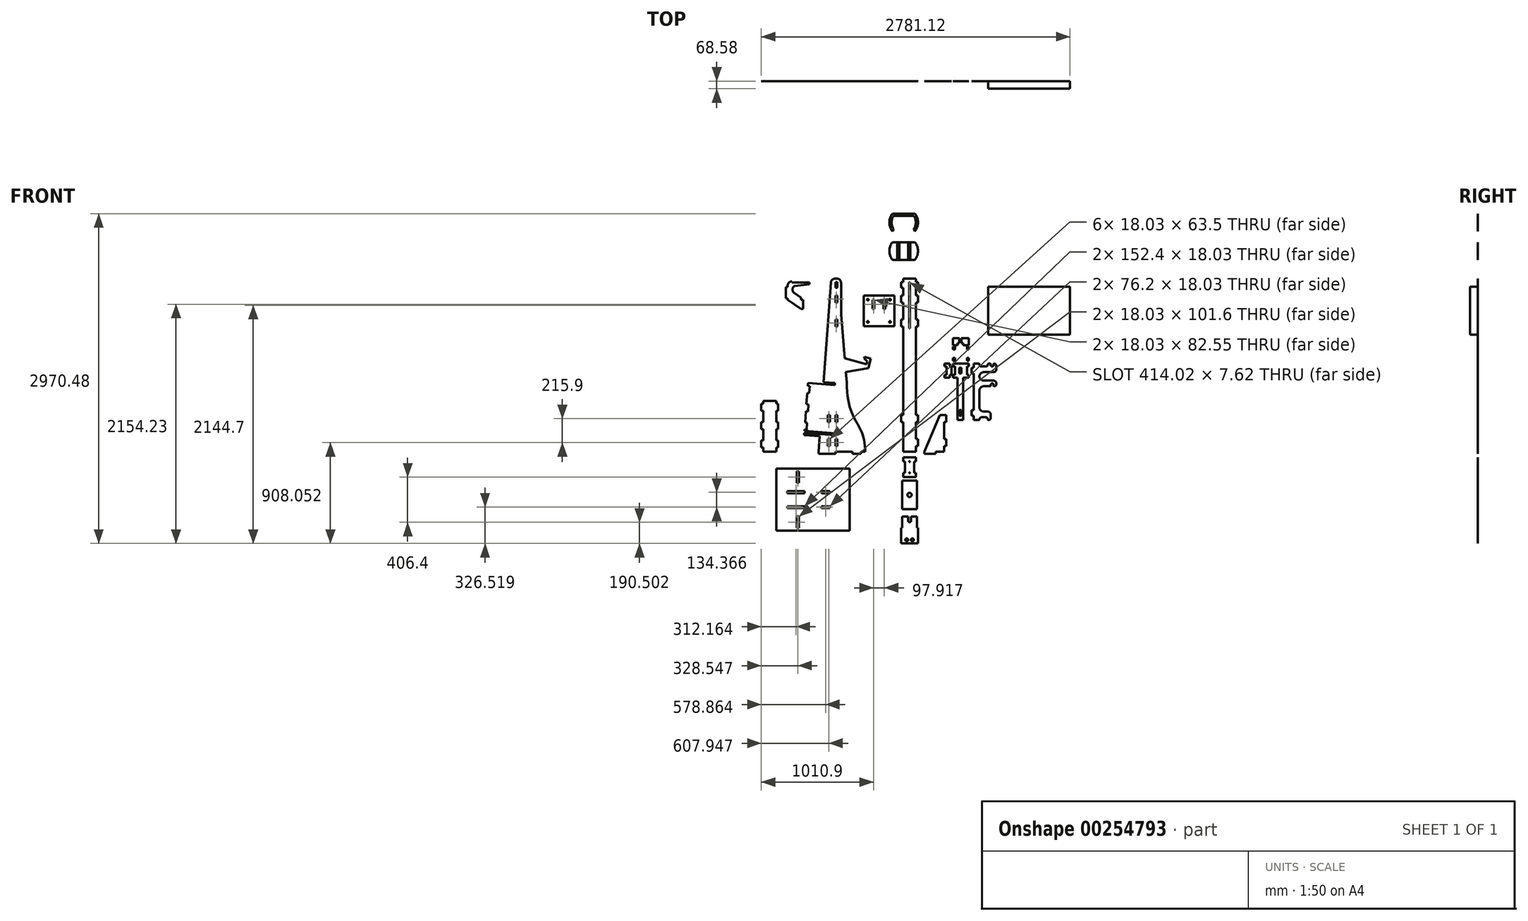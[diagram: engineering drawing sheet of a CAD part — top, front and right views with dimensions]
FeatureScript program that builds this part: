
annotation { "Feature Type Name" : "Feature", "Feature Type Description" : "" }
export const myFeature = defineFeature(function(context is Context, id is Id, definition is map)
    precondition{}
    {
        {
            assignVariable(context, id + "F0", {"name" : "ply34", "anyValue" : .71});
        }
        {
            var Q0;
            Q0=qCreatedBy(makeId("Front.planeOp"),FACE);
            var sketch = newSketch(context, id + "F1", { "sketchPlane" : qUnion([Q0])});
            skLineSegment(sketch, "E0.bottom", {"start": v(-58.17, 729.59) * mm, "end": v(58.17, 729.59) * mm, "construction": true});
            skLineSegment(sketch, "E0.top", {"start": v(-58.17, -729.59) * mm, "end": v(58.17, -729.59) * mm});
            skLineSegment(sketch, "E0.left", {"start": v(-58.17, 729.59) * mm, "end": v(-58.17, -729.59) * mm});
            skLineSegment(sketch, "E0.right", {"start": v(58.17, 729.59) * mm, "end": v(58.17, -729.59) * mm});
            skPoint(sketch, "E0.middle", {"position": v(0, 0) * mm});
            skLineSegment(sketch, "E1.bottom", {"start": v(76.2, 678.79) * mm, "end": v(58.17, 678.79) * mm});
            skLineSegment(sketch, "E1.top", {"start": v(76.2, 615.29) * mm, "end": v(58.17, 615.29) * mm});
            skLineSegment(sketch, "E1.left", {"start": v(58.17, 678.79) * mm, "end": v(58.17, 615.29) * mm});
            skLineSegment(sketch, "E1.right", {"start": v(76.2, 678.79) * mm, "end": v(76.2, 615.29) * mm});
            skPoint(sketch, "E2.oppositeSnap0", {"position": v(76.2, 647.04) * mm});
            skLineSegment(sketch, "E2.bottom", {"start": v(76.2, 462.89) * mm, "end": v(58.17, 462.89) * mm});
            skLineSegment(sketch, "E2.top", {"start": v(76.2, 399.39) * mm, "end": v(58.17, 399.39) * mm});
            skLineSegment(sketch, "E2.left", {"start": v(58.17, 462.89) * mm, "end": v(58.17, 399.39) * mm});
            skLineSegment(sketch, "E2.right", {"start": v(76.2, 462.89) * mm, "end": v(76.2, 399.39) * mm});
            skLineSegment(sketch, "E3", {"start": v(-58.17, 0) * mm, "end": v(58.17, 0) * mm, "construction": true});
            skLineSegment(sketch, "E4", {"start": v(0, 729.59) * mm, "end": v(0, 0) * mm, "construction": true});
            skLineSegment(sketch, "E5.MirrorCS", {"start": v(76.2, -678.79) * mm, "end": v(58.17, -678.79) * mm});
            skLineSegment(sketch, "E6.MirrorCS", {"start": v(76.2, -615.29) * mm, "end": v(58.17, -615.29) * mm});
            skLineSegment(sketch, "E7.MirrorCS", {"start": v(76.2, -462.89) * mm, "end": v(58.17, -462.89) * mm});
            skLineSegment(sketch, "E8.MirrorCS", {"start": v(76.2, -399.39) * mm, "end": v(58.17, -399.39) * mm});
            skPoint(sketch, "E9.MirrorP", {"position": v(76.2, -647.04) * mm});
            skLineSegment(sketch, "E10.MirrorCS", {"start": v(58.17, -678.79) * mm, "end": v(58.17, -615.29) * mm});
            skLineSegment(sketch, "E11.MirrorCS", {"start": v(76.2, -678.79) * mm, "end": v(76.2, -615.29) * mm});
            skLineSegment(sketch, "E12.MirrorCS", {"start": v(76.2, -462.89) * mm, "end": v(76.2, -399.39) * mm});
            skLineSegment(sketch, "E13.MirrorCS", {"start": v(58.17, -462.89) * mm, "end": v(58.17, -399.39) * mm});
            skLineSegment(sketch, "E14.MirrorCS", {"start": v(-76.2, -462.89) * mm, "end": v(-58.17, -462.89) * mm});
            skLineSegment(sketch, "E15.MirrorCS", {"start": v(-58.17, -678.79) * mm, "end": v(-58.17, -615.29) * mm});
            skLineSegment(sketch, "E16.MirrorCS", {"start": v(-76.2, 462.89) * mm, "end": v(-76.2, 399.39) * mm});
            skLineSegment(sketch, "E17.MirrorCS", {"start": v(-58.17, 462.89) * mm, "end": v(-58.17, 399.39) * mm});
            skLineSegment(sketch, "E18.MirrorCS", {"start": v(-76.2, 399.39) * mm, "end": v(-58.17, 399.39) * mm});
            skLineSegment(sketch, "E19.MirrorCS", {"start": v(-76.2, 462.89) * mm, "end": v(-58.17, 462.89) * mm});
            skLineSegment(sketch, "E20.MirrorCS", {"start": v(-76.2, 678.79) * mm, "end": v(-76.2, 615.29) * mm});
            skLineSegment(sketch, "E21.MirrorCS", {"start": v(-58.17, 678.79) * mm, "end": v(-58.17, 615.29) * mm});
            skLineSegment(sketch, "E22.MirrorCS", {"start": v(-76.2, -615.29) * mm, "end": v(-58.17, -615.29) * mm});
            skLineSegment(sketch, "E23.MirrorCS", {"start": v(-76.2, -678.79) * mm, "end": v(-58.17, -678.79) * mm});
            skLineSegment(sketch, "E24.MirrorCS", {"start": v(-76.2, 615.29) * mm, "end": v(-58.17, 615.29) * mm});
            skLineSegment(sketch, "E25.MirrorCS", {"start": v(-76.2, -399.39) * mm, "end": v(-58.17, -399.39) * mm});
            skLineSegment(sketch, "E26.MirrorCS", {"start": v(-76.2, -678.79) * mm, "end": v(-76.2, -615.29) * mm});
            skLineSegment(sketch, "E27.MirrorCS", {"start": v(-76.2, 678.79) * mm, "end": v(-58.17, 678.79) * mm});
            skLineSegment(sketch, "E28.MirrorCS", {"start": v(-76.2, -462.89) * mm, "end": v(-76.2, -399.39) * mm});
            skPoint(sketch, "E29.MirrorP", {"position": v(-76.2, -647.04) * mm});
            skPoint(sketch, "E30.MirrorP", {"position": v(-76.2, 647.04) * mm});
            skLineSegment(sketch, "E31.MirrorCS", {"start": v(-58.17, -462.89) * mm, "end": v(-58.17, -399.39) * mm});
            skLineSegment(sketch, "E32", {"start": v(-667.77, 729.59) * mm, "end": v(-712.22, 729.59) * mm, "construction": true});
            skLineSegment(sketch, "E33", {"start": v(-712.22, 729.59) * mm, "end": v(-820.17, -729.59) * mm});
            skLineSegment(sketch, "E34", {"start": v(-820.17, -729.59) * mm, "end": v(-667.77, -729.59) * mm});
            skLineSegment(sketch, "E35", {"start": v(-667.77, -729.59) * mm, "end": v(-667.77, 729.59) * mm, "construction": true});
            skLineSegment(sketch, "E36", {"start": v(-667.77, -678.79) * mm, "end": v(-649.73, -678.79) * mm});
            skLineSegment(sketch, "E37", {"start": v(-649.73, -678.79) * mm, "end": v(-649.73, -615.29) * mm});
            skLineSegment(sketch, "E38", {"start": v(-649.73, -615.29) * mm, "end": v(-667.77, -615.29) * mm});
            skLineSegment(sketch, "E39", {"start": v(-667.77, -462.89) * mm, "end": v(-649.73, -462.89) * mm});
            skLineSegment(sketch, "E40", {"start": v(-649.73, -462.89) * mm, "end": v(-649.73, -399.39) * mm});
            skLineSegment(sketch, "E41", {"start": v(-649.73, -399.39) * mm, "end": v(-667.77, -399.39) * mm});
            skLineSegment(sketch, "E42.MirrorCS", {"start": v(-667.77, 678.79) * mm, "end": v(-649.73, 678.79) * mm});
            skLineSegment(sketch, "E43.MirrorCS", {"start": v(-649.73, 399.39) * mm, "end": v(-667.77, 399.39) * mm});
            skLineSegment(sketch, "E44.MirrorCS", {"start": v(-667.77, 462.89) * mm, "end": v(-649.73, 462.89) * mm});
            skLineSegment(sketch, "E45.MirrorCS", {"start": v(-649.73, 615.29) * mm, "end": v(-667.77, 615.29) * mm});
            skLineSegment(sketch, "E46.MirrorCS", {"start": v(-649.73, 678.79) * mm, "end": v(-649.73, 615.29) * mm});
            skLineSegment(sketch, "E47.MirrorCS", {"start": v(-649.73, 462.89) * mm, "end": v(-649.73, 399.39) * mm});
            skLineSegment(sketch, "E48.bottom", {"start": v(-718.57, -462.89) * mm, "end": v(-736.6, -462.89) * mm});
            skLineSegment(sketch, "E48.top", {"start": v(-718.57, -399.39) * mm, "end": v(-736.6, -399.39) * mm});
            skLineSegment(sketch, "E48.left", {"start": v(-718.57, -462.89) * mm, "end": v(-718.57, -399.39) * mm});
            skLineSegment(sketch, "E48.right", {"start": v(-736.6, -462.89) * mm, "end": v(-736.6, -399.39) * mm});
            skPoint(sketch, "E48.middle", {"position": v(-727.58, -431.14) * mm});
            skPoint(sketch, "E48.middle.positionSnap0", {"position": v(-649.73, -431.14) * mm});
            skPoint(sketch, "E48.middle.positionSnap1", {"position": v(-743.97, -729.59) * mm});
            skPoint(sketch, "E48.centerSnap0", {"position": v(-649.73, -431.14) * mm});
            skPoint(sketch, "E48.centerSnap1", {"position": v(-743.97, -729.59) * mm});
            skLineSegment(sketch, "E49.bottom", {"start": v(-718.57, -615.29) * mm, "end": v(-736.6, -615.29) * mm});
            skLineSegment(sketch, "E49.top", {"start": v(-718.57, -678.79) * mm, "end": v(-736.6, -678.79) * mm});
            skLineSegment(sketch, "E49.left", {"start": v(-718.57, -615.29) * mm, "end": v(-718.57, -678.79) * mm});
            skLineSegment(sketch, "E49.right", {"start": v(-736.6, -615.29) * mm, "end": v(-736.6, -678.79) * mm});
            skPoint(sketch, "E49.middle", {"position": v(-727.58, -647.04) * mm});
            skPoint(sketch, "E49.middle.positionSnap0", {"position": v(-649.73, -647.04) * mm});
            skPoint(sketch, "E49.cornerSnap0", {"position": v(-718.57, -431.14) * mm});
            skPoint(sketch, "E49.centerSnap0", {"position": v(-649.73, -647.04) * mm});
            skLineSegment(sketch, "E50", {"start": v(-793.93, -374.96) * mm, "end": v(-775.95, -376.29) * mm, "construction": true});
            skLineSegment(sketch, "E51", {"start": v(-775.95, -376.29) * mm, "end": v(-771.26, -312.96) * mm, "construction": true});
            skLineSegment(sketch, "E52", {"start": v(-771.26, -312.96) * mm, "end": v(-789.25, -311.63) * mm, "construction": true});
            skLineSegment(sketch, "E53", {"start": v(-781.75, -210.3) * mm, "end": v(-763.76, -211.64) * mm, "construction": true});
            skLineSegment(sketch, "E54", {"start": v(-763.76, -211.64) * mm, "end": v(-759.08, -148.31) * mm, "construction": true});
            skLineSegment(sketch, "E55", {"start": v(-759.08, -148.31) * mm, "end": v(-777.06, -146.98) * mm, "construction": true});
            skLineSegment(sketch, "E56.bottom", {"start": v(-1201.17, -729.59) * mm, "end": v(-1317.5, -729.59) * mm});
            skLineSegment(sketch, "E56.top", {"start": v(-1201.17, -272.39) * mm, "end": v(-1317.5, -272.39) * mm});
            skLineSegment(sketch, "E56.left", {"start": v(-1201.17, -729.59) * mm, "end": v(-1201.17, -272.39) * mm});
            skLineSegment(sketch, "E56.right", {"start": v(-1317.5, -729.59) * mm, "end": v(-1317.5, -272.39) * mm});
            skLineSegment(sketch, "E57.bottom", {"start": v(-1183.13, -526.39) * mm, "end": v(-1201.17, -526.39) * mm});
            skLineSegment(sketch, "E57.top", {"start": v(-1183.13, -462.89) * mm, "end": v(-1201.17, -462.89) * mm});
            skLineSegment(sketch, "E57.right", {"start": v(-1183.13, -526.39) * mm, "end": v(-1183.13, -462.89) * mm});
            skLineSegment(sketch, "E58", {"start": v(-1259.33, -272.39) * mm, "end": v(-1259.33, -729.59) * mm, "construction": true});
            skLineSegment(sketch, "E59.MirrorCS", {"start": v(-1183.13, -297.79) * mm, "end": v(-1201.17, -297.79) * mm});
            skLineSegment(sketch, "E60.MirrorCS", {"start": v(-1183.13, -297.79) * mm, "end": v(-1183.13, -361.29) * mm});
            skLineSegment(sketch, "E61.MirrorCS", {"start": v(-1183.13, -361.29) * mm, "end": v(-1201.17, -361.29) * mm});
            skLineSegment(sketch, "E62.MirrorCS", {"start": v(-1335.53, -526.39) * mm, "end": v(-1335.53, -462.89) * mm});
            skLineSegment(sketch, "E63.MirrorCS", {"start": v(-1335.53, -462.89) * mm, "end": v(-1317.5, -462.89) * mm});
            skLineSegment(sketch, "E64.MirrorCS", {"start": v(-1335.53, -361.29) * mm, "end": v(-1317.5, -361.29) * mm});
            skLineSegment(sketch, "E65.MirrorCS", {"start": v(-1335.53, -526.39) * mm, "end": v(-1317.5, -526.39) * mm});
            skLineSegment(sketch, "E66.MirrorCS", {"start": v(-1335.53, -297.79) * mm, "end": v(-1335.53, -361.29) * mm});
            skLineSegment(sketch, "E67.MirrorCS", {"start": v(-1335.53, -297.79) * mm, "end": v(-1317.5, -297.79) * mm});
            skLineSegment(sketch, "E68", {"start": v(312.17, -399.39) * mm, "end": v(274.07, -399.39) * mm});
            skLineSegment(sketch, "E69", {"start": v(274.07, -399.39) * mm, "end": v(134.37, -729.59) * mm});
            skLineSegment(sketch, "E70", {"start": v(134.37, -729.59) * mm, "end": v(312.17, -729.59) * mm});
            skLineSegment(sketch, "E71", {"start": v(312.17, -729.59) * mm, "end": v(312.17, -399.39) * mm});
            skLineSegment(sketch, "E72", {"start": v(312.17, -399.39) * mm, "end": v(330.2, -399.39) * mm});
            skLineSegment(sketch, "E73", {"start": v(330.2, -399.39) * mm, "end": v(330.2, -462.89) * mm});
            skLineSegment(sketch, "E74", {"start": v(330.2, -462.89) * mm, "end": v(312.17, -462.89) * mm});
            skLineSegment(sketch, "E75", {"start": v(312.17, -615.29) * mm, "end": v(330.2, -615.29) * mm});
            skLineSegment(sketch, "E76", {"start": v(330.2, -615.29) * mm, "end": v(330.2, -678.79) * mm});
            skLineSegment(sketch, "E77", {"start": v(330.2, -678.79) * mm, "end": v(312.17, -678.79) * mm});
            skLineSegment(sketch, "E78", {"start": v(-667.77, 729.59) * mm, "end": v(-629.67, 729.59) * mm, "construction": true});
            skLineSegment(sketch, "E79", {"start": v(-712.22, 729.59) * mm, "end": v(-707.33, 795.62) * mm});
            skLineSegment(sketch, "E80", {"start": v(-669.33, 830.91) * mm, "end": v(-464.57, 830.91) * mm, "construction": true});
            skLineSegment(sketch, "E81", {"start": v(-464.57, 830.91) * mm, "end": v(-464.57, 780.11) * mm, "construction": true});
            skLineSegment(sketch, "E82", {"start": v(-464.57, 780.11) * mm, "end": v(-616.97, 761.06) * mm, "construction": true});
            skLineSegment(sketch, "E83", {"start": v(-509.38, 438.81) * mm, "end": v(-475.02, 438.81) * mm, "construction": true});
            skLineSegment(sketch, "E84", {"start": v(-616.97, 761.06) * mm, "end": v(-616.97, 659.46) * mm});
            skLineSegment(sketch, "E85", {"start": v(-616.97, 659.46) * mm, "end": v(-515.37, 659.46) * mm, "construction": true});
            skLineSegment(sketch, "E86.bottom", {"start": v(-515.37, 659.46) * mm, "end": v(-533.4, 659.46) * mm, "construction": true});
            skLineSegment(sketch, "E86.top", {"start": v(-515.37, 640.41) * mm, "end": v(-533.4, 640.41) * mm, "construction": true});
            skLineSegment(sketch, "E86.left", {"start": v(-515.37, 659.46) * mm, "end": v(-515.37, 640.41) * mm, "construction": true});
            skLineSegment(sketch, "E86.right", {"start": v(-533.4, 659.46) * mm, "end": v(-533.4, 640.41) * mm, "construction": true});
            skLineSegment(sketch, "E87", {"start": v(-515.37, 659.46) * mm, "end": v(-515.37, 557.86) * mm, "construction": true});
            skLineSegment(sketch, "E88", {"start": v(-616.97, 507.06) * mm, "end": v(-566.17, -102.54) * mm});
            skPoint(sketch, "E88.endSnap0", {"position": v(-566.17, 659.46) * mm});
            skLineSegment(sketch, "E89.0", {"start": v(-547.12, 586.68) * mm, "end": v(-616.97, 544.22) * mm, "construction": true});
            skLineSegment(sketch, "E89.1", {"start": v(-547.12, 627.71) * mm, "end": v(-547.12, 586.68) * mm, "construction": true});
            skLineSegment(sketch, "E89.2", {"start": v(-616.97, 627.71) * mm, "end": v(-547.12, 627.71) * mm, "construction": true});
            skLineSegment(sketch, "E90", {"start": v(-616.97, 627.71) * mm, "end": v(-616.97, 544.22) * mm});
            skLineSegment(sketch, "E91", {"start": v(-667.77, 678.79) * mm, "end": v(-667.77, 615.29) * mm});
            skLineSegment(sketch, "E92", {"start": v(-667.77, 462.89) * mm, "end": v(-667.77, 399.39) * mm});
            skLineSegment(sketch, "E93", {"start": v(-667.77, -399.39) * mm, "end": v(-667.77, -462.89) * mm});
            skLineSegment(sketch, "E94", {"start": v(-667.77, -615.29) * mm, "end": v(-667.77, -678.79) * mm});
            skLineSegment(sketch, "E95", {"start": v(-667.77, -729.59) * mm, "end": v(-439.17, -729.59) * mm});
            skLineSegment(sketch, "E96", {"start": v(-583.98, 111.27) * mm, "end": v(-387.7, 58.68) * mm});
            skLineSegment(sketch, "E97", {"start": v(-387.7, 58.68) * mm, "end": v(-381.13, 83.21) * mm});
            skLineSegment(sketch, "E98", {"start": v(-370.57, 24.5) * mm, "end": v(-576.75, 24.5) * mm, "construction": true});
            skLineSegment(sketch, "E99", {"start": v(-370.57, 24.5) * mm, "end": v(-573.77, -11.33) * mm});
            skLineSegment(sketch, "E100.bottom", {"start": v(-375.67, 640.41) * mm, "end": v(-175.67, 640.41) * mm, "construction": true});
            skLineSegment(sketch, "E100.top", {"start": v(-375.67, 440.41) * mm, "end": v(-175.67, 440.41) * mm, "construction": true});
            skLineSegment(sketch, "E100.left", {"start": v(-375.67, 640.41) * mm, "end": v(-375.67, 440.41) * mm, "construction": true});
            skLineSegment(sketch, "E100.right", {"start": v(-175.67, 640.41) * mm, "end": v(-175.67, 440.41) * mm, "construction": true});
            skLineSegment(sketch, "E101.0", {"start": v(-413.77, 678.51) * mm, "end": v(-137.57, 678.51) * mm});
            skLineSegment(sketch, "E101.1", {"start": v(-413.77, 678.51) * mm, "end": v(-413.77, 402.31) * mm});
            skLineSegment(sketch, "E101.2", {"start": v(-413.77, 402.31) * mm, "end": v(-137.57, 402.31) * mm});
            skLineSegment(sketch, "E101.3", {"start": v(-137.57, 678.51) * mm, "end": v(-137.57, 402.31) * mm});
            skLineSegment(sketch, "E102", {"start": v(-515.37, 557.86) * mm, "end": v(-533.4, 557.86) * mm, "construction": true});
            skLineSegment(sketch, "E103", {"start": v(-533.4, 557.86) * mm, "end": v(-616.97, 507.06) * mm, "construction": true});
            skLineSegment(sketch, "E104.bottom", {"start": v(-333.64, 640.41) * mm, "end": v(-315.6, 640.41) * mm});
            skLineSegment(sketch, "E104.top", {"start": v(-333.64, 557.86) * mm, "end": v(-315.6, 557.86) * mm});
            skLineSegment(sketch, "E104.left", {"start": v(-333.64, 640.41) * mm, "end": v(-333.64, 557.86) * mm});
            skLineSegment(sketch, "E104.right", {"start": v(-315.6, 640.41) * mm, "end": v(-315.6, 557.86) * mm});
            skLineSegment(sketch, "E105", {"start": v(-275.67, 678.51) * mm, "end": v(-275.67, 440.41) * mm, "construction": true});
            skLineSegment(sketch, "E106.MirrorCS", {"start": v(-217.7, 640.41) * mm, "end": v(-235.72, 640.41) * mm});
            skLineSegment(sketch, "E107.MirrorCS", {"start": v(-235.72, 640.41) * mm, "end": v(-235.72, 557.86) * mm});
            skLineSegment(sketch, "E108.MirrorCS", {"start": v(-217.7, 640.41) * mm, "end": v(-217.7, 557.86) * mm});
            skLineSegment(sketch, "E109.MirrorCS", {"start": v(-217.7, 557.86) * mm, "end": v(-235.72, 557.86) * mm});
            skCircle(sketch, "E110", {"center": v(-375.67, 640.41) * mm, "radius": 6.99 * mm});
            skLineSegment(sketch, "E111", {"start": v(-375.67, 540.41) * mm, "end": v(-175.67, 540.41) * mm, "construction": true});
            skCircle(sketch, "E112.MirrorC", {"center": v(-175.67, 640.41) * mm, "radius": 6.99 * mm});
            skCircle(sketch, "E113.MirrorC", {"center": v(-375.67, 440.41) * mm, "radius": 6.99 * mm});
            skCircle(sketch, "E114.MirrorC", {"center": v(-175.67, 440.41) * mm, "radius": 6.99 * mm});
            skLineSegment(sketch, "E115.bottom", {"start": v(-582.04, 830.91) * mm, "end": v(-505.84, 830.91) * mm, "construction": true});
            skLineSegment(sketch, "E115.top", {"start": v(-582.04, 848.95) * mm, "end": v(-505.84, 848.95) * mm, "construction": true});
            skLineSegment(sketch, "E115.left", {"start": v(-582.04, 848.95) * mm, "end": v(-582.04, 830.91) * mm});
            skLineSegment(sketch, "E115.right", {"start": v(-505.84, 848.95) * mm, "end": v(-505.84, 830.91) * mm, "construction": true});
            skLineSegment(sketch, "E116.bottom", {"start": v(-180.97, 983.59) * mm, "end": v(76.2, 983.59) * mm});
            skLineSegment(sketch, "E116.top", {"start": v(-180.97, 1174.09) * mm, "end": v(76.2, 1174.09) * mm});
            skLineSegment(sketch, "E116.left", {"start": v(-180.97, 983.59) * mm, "end": v(-180.97, 1174.09) * mm});
            skLineSegment(sketch, "E116.right", {"start": v(76.2, 983.59) * mm, "end": v(76.2, 1174.09) * mm});
            skLineSegment(sketch, "E117.bottom", {"start": v(-110.36, 1158.21) * mm, "end": v(-92.33, 1158.21) * mm});
            skLineSegment(sketch, "E117.top", {"start": v(-110.36, 999.46) * mm, "end": v(-92.33, 999.46) * mm});
            skLineSegment(sketch, "E117.left", {"start": v(-110.36, 1158.21) * mm, "end": v(-110.36, 999.46) * mm});
            skLineSegment(sketch, "E117.right", {"start": v(-92.33, 1158.21) * mm, "end": v(-92.33, 999.46) * mm});
            skPoint(sketch, "E118.oppositeSnap0", {"position": v(-101.35, 999.46) * mm});
            skLineSegment(sketch, "E118.bottom", {"start": v(-12.45, 1158.21) * mm, "end": v(5.59, 1158.21) * mm});
            skLineSegment(sketch, "E118.top", {"start": v(-12.45, 999.46) * mm, "end": v(5.59, 999.46) * mm});
            skLineSegment(sketch, "E118.left", {"start": v(-12.45, 1158.21) * mm, "end": v(-12.45, 999.46) * mm});
            skLineSegment(sketch, "E118.right", {"start": v(5.59, 1158.21) * mm, "end": v(5.59, 999.46) * mm});
            skLineSegment(sketch, "E119", {"start": v(-92.33, 1078.84) * mm, "end": v(-12.45, 1078.84) * mm, "construction": true});
            skPoint(sketch, "E120", {"position": v(-52.39, 1078.84) * mm});
            skPoint(sketch, "E121", {"position": v(-52.39, 1174.09) * mm});
            skPoint(sketch, "E122", {"position": v(-180.97, 1078.84) * mm});
            skArc(sketch, "E123", {"start": v(-143.82, 1396.34) * mm, "mid": v(-161.92, 1336.01) * mm, "end": v(-143.82, 1275.69) * mm});
            skLineSegment(sketch, "E124.bottom", {"start": v(-143.82, 1396.34) * mm, "end": v(39.04, 1396.34) * mm});
            skLineSegment(sketch, "E124.top", {"start": v(-143.82, 1275.69) * mm, "end": v(39.04, 1275.69) * mm});
            skLineSegment(sketch, "E124.left", {"start": v(-143.82, 1396.34) * mm, "end": v(-143.82, 1275.69) * mm});
            skLineSegment(sketch, "E124.right", {"start": v(39.04, 1396.34) * mm, "end": v(39.04, 1275.69) * mm});
            skArc(sketch, "E125.trimOffspring", {"start": v(39.04, 1275.69) * mm, "mid": v(57.15, 1336.01) * mm, "end": v(39.04, 1396.34) * mm});
            skArc(sketch, "E126.0", {"start": v(-153.55, 1415.39) * mm, "mid": v(-180.97, 1336.01) * mm, "end": v(-153.55, 1256.64) * mm});
            skLineSegment(sketch, "E126.1", {"start": v(-153.55, 1415.39) * mm, "end": v(48.78, 1415.39) * mm});
            skArc(sketch, "E126.2", {"start": v(48.78, 1256.64) * mm, "mid": v(76.2, 1336.01) * mm, "end": v(48.78, 1415.39) * mm});
            skLineSegment(sketch, "E126.3", {"start": v(-153.55, 1256.64) * mm, "end": v(48.78, 1256.64) * mm});
            skPoint(sketch, "E127", {"position": v(-180.97, 1336.01) * mm});
            skLineSegment(sketch, "E128", {"start": v(-52.39, 1256.64) * mm, "end": v(-52.39, 1174.09) * mm, "construction": true});
            skLineSegment(sketch, "E129", {"start": v(-64.97, 1207.43) * mm, "end": v(-153.55, 1207.43) * mm, "construction": true});
            skLineSegment(sketch, "E130.MirrorCS", {"start": v(-153.55, 999.46) * mm, "end": v(48.78, 999.46) * mm});
            skArc(sketch, "E131.MirrorCS", {"start": v(-153.55, 999.46) * mm, "mid": v(-180.97, 1078.84) * mm, "end": v(-153.55, 1158.21) * mm});
            skArc(sketch, "E132.MirrorCS", {"start": v(48.78, 1158.21) * mm, "mid": v(76.2, 1078.84) * mm, "end": v(48.78, 999.46) * mm});
            skLineSegment(sketch, "E133.MirrorCS", {"start": v(-153.55, 1158.21) * mm, "end": v(48.78, 1158.21) * mm});
            skLineSegment(sketch, "E134", {"start": v(-52.39, 1158.21) * mm, "end": v(-52.39, 999.46) * mm, "construction": true});
            skLineSegment(sketch, "E135.bottom", {"start": v(708.99, 756.31) * mm, "end": v(1445.59, 756.31) * mm});
            skLineSegment(sketch, "E135.top", {"start": v(708.99, 324.51) * mm, "end": v(1445.59, 324.51) * mm});
            skLineSegment(sketch, "E135.left", {"start": v(708.99, 756.31) * mm, "end": v(708.99, 324.51) * mm});
            skLineSegment(sketch, "E135.right", {"start": v(1445.59, 756.31) * mm, "end": v(1445.59, 324.51) * mm});
            skPoint(sketch, "E136", {"position": v(708.99, 540.41) * mm});
            skLineSegment(sketch, "E137", {"start": v(-515.37, 756.31) * mm, "end": v(-464.57, 756.31) * mm, "construction": true});
            skPoint(sketch, "E138.visualSharp", {"position": v(-704.72, 830.91) * mm});
            skArc(sketch, "E138.filletArc", {"start": v(-669.33, 830.91) * mm, "mid": v(-695.26, 820.73) * mm, "end": v(-707.33, 795.62) * mm});
            skLineSegment(sketch, "E139", {"start": v(-775.95, -376.29) * mm, "end": v(-802.08, -729.59) * mm, "construction": true});
            skPoint(sketch, "E140", {"position": v(0, -729.59) * mm});
            skLineSegment(sketch, "E141", {"start": v(-1032.97, -526.39) * mm, "end": v(-1032.97, -703.96) * mm, "construction": true});
            skLineSegment(sketch, "E142", {"start": v(-793.93, -374.96) * mm, "end": v(-800.93, -374.44) * mm, "construction": true});
            skLineSegment(sketch, "E143", {"start": v(-759.08, -148.31) * mm, "end": v(-757.2, -122.98) * mm, "construction": true});
            skLineSegment(sketch, "E144", {"start": v(-757.2, -122.98) * mm, "end": v(-775.2, -121.65) * mm, "construction": true});
            skLineSegment(sketch, "E145", {"start": v(-775.2, -121.65) * mm, "end": v(-673.87, -129.15) * mm});
            skLineSegment(sketch, "E146", {"start": v(-673.87, -129.15) * mm, "end": v(-672.54, -111.16) * mm});
            skLineSegment(sketch, "E147", {"start": v(-672.54, -111.16) * mm, "end": v(-773.86, -103.66) * mm});
            skLineSegment(sketch, "E148", {"start": v(-773.86, -103.66) * mm, "end": v(-775.2, -121.65) * mm});
            skLineSegment(sketch, "E149.bottom", {"start": v(-67, -1313.79) * mm, "end": v(67.37, -1313.79) * mm});
            skLineSegment(sketch, "E149.top", {"start": v(-67, -1555.09) * mm, "end": v(67.37, -1555.09) * mm});
            skLineSegment(sketch, "E149.left", {"start": v(-67, -1313.79) * mm, "end": v(-67, -1555.09) * mm});
            skLineSegment(sketch, "E149.right", {"start": v(67.37, -1313.79) * mm, "end": v(67.37, -1555.09) * mm});
            skPoint(sketch, "E150", {"position": v(0.2, -1313.79) * mm});
            skLineSegment(sketch, "E151.bottom", {"start": v(-12.5, -1313.79) * mm, "end": v(12.9, -1313.79) * mm});
            skLineSegment(sketch, "E151.top", {"start": v(-12.5, -1351.89) * mm, "end": v(12.9, -1351.89) * mm, "construction": true});
            skLineSegment(sketch, "E151.left", {"start": v(-12.5, -1313.79) * mm, "end": v(-12.5, -1351.89) * mm});
            skLineSegment(sketch, "E151.right", {"start": v(12.9, -1313.79) * mm, "end": v(12.9, -1351.89) * mm});
            skPoint(sketch, "E151.middle", {"position": v(0.2, -1332.84) * mm});
            skCircle(sketch, "E152", {"center": v(0.2, -1351.89) * mm, "radius": 12.7 * mm});
            skCircle(sketch, "E153", {"center": v(-25.2, -1523.34) * mm, "radius": 12.7 * mm});
            skCircle(sketch, "E154", {"center": v(25.6, -1523.34) * mm, "radius": 12.7 * mm});
            skLineSegment(sketch, "E155", {"start": v(-25.2, -1523.34) * mm, "end": v(25.6, -1523.34) * mm, "construction": true});
            skPoint(sketch, "E156", {"position": v(0.2, -1523.34) * mm});
            skLineSegment(sketch, "E157", {"start": v(-381.13, 83.21) * mm, "end": v(-409.12, 113.72) * mm});
            skLineSegment(sketch, "E158", {"start": v(-409.12, 113.72) * mm, "end": v(-405.83, 125.99) * mm});
            skLineSegment(sketch, "E159", {"start": v(-405.83, 125.99) * mm, "end": v(-347.56, 110.37) * mm});
            skLineSegment(sketch, "E160", {"start": v(-370.57, 24.5) * mm, "end": v(-347.56, 110.37) * mm});
            skLineSegment(sketch, "E161", {"start": v(-153.55, 1256.64) * mm, "end": v(-143.82, 1275.69) * mm});
            skLineSegment(sketch, "E162", {"start": v(39.04, 1275.69) * mm, "end": v(48.78, 1256.64) * mm});
            skLineSegment(sketch, "E163", {"start": v(-976.26, 659.46) * mm, "end": v(-1041.15, 702.72) * mm});
            skLineSegment(sketch, "E164", {"start": v(-976.26, 659.46) * mm, "end": v(-976.26, 640.41) * mm});
            skLineSegment(sketch, "E165", {"start": v(-976.26, 640.41) * mm, "end": v(-958.23, 640.41) * mm});
            skLineSegment(sketch, "E166", {"start": v(-958.23, 640.41) * mm, "end": v(-958.23, 557.86) * mm});
            skLineSegment(sketch, "E167", {"start": v(-958.23, 557.86) * mm, "end": v(-976.26, 557.86) * mm});
            skLineSegment(sketch, "E168", {"start": v(-976.26, 557.86) * mm, "end": v(-1096.9, 638.3) * mm});
            skLineSegment(sketch, "E169", {"start": v(-1052.46, 723.86) * mm, "end": v(-1052.46, 738.64) * mm});
            skLineSegment(sketch, "E170", {"start": v(-1030.2, 763.84) * mm, "end": v(-900.06, 780.11) * mm});
            skLineSegment(sketch, "E171", {"start": v(-900.06, 780.11) * mm, "end": v(-900.06, 805.51) * mm});
            skLineSegment(sketch, "E172", {"start": v(-900.06, 805.51) * mm, "end": v(-1058.8, 805.51) * mm});
            skLineSegment(sketch, "E173", {"start": v(-1096.9, 767.41) * mm, "end": v(-1096.9, 638.3) * mm});
            skPoint(sketch, "E174.visualSharp", {"position": v(-1096.9, 805.51) * mm});
            skArc(sketch, "E174.filletArc", {"start": v(-1058.8, 805.51) * mm, "mid": v(-1085.75, 794.35) * mm, "end": v(-1096.9, 767.41) * mm});
            skPoint(sketch, "E175.visualSharp", {"position": v(-1052.46, 761.06) * mm});
            skArc(sketch, "E175.filletArc", {"start": v(-1030.2, 763.84) * mm, "mid": v(-1046.1, 755.45) * mm, "end": v(-1052.46, 738.64) * mm});
            skPoint(sketch, "E176.visualSharp", {"position": v(-1052.46, 710.26) * mm});
            skArc(sketch, "E176.filletArc", {"start": v(-1052.46, 723.86) * mm, "mid": v(-1049.45, 711.87) * mm, "end": v(-1041.15, 702.72) * mm});
            skLineSegment(sketch, "E177.bottom", {"start": v(-1058.8, 805.51) * mm, "end": v(-900.06, 805.51) * mm});
            skLineSegment(sketch, "E177.top", {"start": v(-1058.8, 796.5) * mm, "end": v(-900.06, 796.5) * mm});
            skLineSegment(sketch, "E177.left", {"start": v(-1058.8, 805.51) * mm, "end": v(-1058.8, 796.5) * mm});
            skLineSegment(sketch, "E177.right", {"start": v(-900.06, 805.51) * mm, "end": v(-900.06, 796.5) * mm});
            skLineSegment(sketch, "E178", {"start": v(-616.97, 659.46) * mm, "end": v(-616.97, 507.06) * mm});
            skLineSegment(sketch, "E179", {"start": v(-616.97, 761.06) * mm, "end": v(-616.97, 792.81) * mm});
            skLineSegment(sketch, "E180", {"start": v(-1096.9, 752.6) * mm, "end": v(-1114.94, 752.6) * mm});
            skLineSegment(sketch, "E181", {"start": v(-1114.94, 752.6) * mm, "end": v(-1114.94, 651) * mm});
            skLineSegment(sketch, "E182", {"start": v(-1114.94, 651) * mm, "end": v(-1096.9, 651) * mm});
            skLineSegment(sketch, "E183.bottom", {"start": v(-57.78, -780.39) * mm, "end": v(58.17, -780.39) * mm});
            skLineSegment(sketch, "E183.top", {"start": v(-57.78, -958.19) * mm, "end": v(58.17, -958.19) * mm});
            skLineSegment(sketch, "E183.left", {"start": v(-57.79, -780.39) * mm, "end": v(-57.79, -958.19) * mm});
            skLineSegment(sketch, "E183.right", {"start": v(58.17, -780.39) * mm, "end": v(58.17, -958.19) * mm});
            skLineSegment(sketch, "E184", {"start": v(-110.36, 1046.28) * mm, "end": v(5.59, 1046.28) * mm, "construction": true});
            skLineSegment(sketch, "E185.bottom", {"start": v(-57.78, -818.49) * mm, "end": v(-39.75, -818.49) * mm});
            skLineSegment(sketch, "E185.top", {"start": v(-57.78, -920.09) * mm, "end": v(-39.75, -920.09) * mm});
            skLineSegment(sketch, "E185.left", {"start": v(-57.79, -818.49) * mm, "end": v(-57.79, -920.09) * mm});
            skLineSegment(sketch, "E185.right", {"start": v(-39.75, -818.49) * mm, "end": v(-39.75, -920.09) * mm});
            skPoint(sketch, "E186", {"position": v(-57.78, -869.29) * mm});
            skCircle(sketch, "E187", {"center": v(0.2, -818.49) * mm, "radius": 3.81 * mm});
            skCircle(sketch, "E188", {"center": v(0.2, -920.09) * mm, "radius": 3.81 * mm});
            skLineSegment(sketch, "E189", {"start": v(0, 792.81) * mm, "end": v(0, 386.41) * mm});
            skArc(sketch, "E190.0.startCap", {"start": v(-3.81, 792.81) * mm, "mid": v(0, 796.62) * mm, "end": v(3.8, 792.81) * mm});
            skArc(sketch, "E190.0.endCap", {"start": v(3.8, 386.41) * mm, "mid": v(0, 382.6) * mm, "end": v(-3.81, 386.41) * mm});
            skLineSegment(sketch, "E190.0.left", {"start": v(3.8, 792.81) * mm, "end": v(3.8, 386.41) * mm});
            skLineSegment(sketch, "E190.0.right", {"start": v(-3.81, 792.81) * mm, "end": v(-3.81, 386.41) * mm});
            skLineSegment(sketch, "E191", {"start": v(0.2, -958.19) * mm, "end": v(0.2, -780.39) * mm, "construction": true});
            skLineSegment(sketch, "E192.MirrorCS", {"start": v(58.17, -818.49) * mm, "end": v(40.13, -818.49) * mm});
            skLineSegment(sketch, "E193.MirrorCS", {"start": v(58.17, -920.09) * mm, "end": v(40.13, -920.09) * mm});
            skLineSegment(sketch, "E194.MirrorCS", {"start": v(40.13, -818.49) * mm, "end": v(40.13, -920.09) * mm});
            skLineSegment(sketch, "E195.MirrorCS", {"start": v(58.17, -818.49) * mm, "end": v(58.17, -920.09) * mm});
            skPoint(sketch, "E196.MirrorP", {"position": v(58.17, -869.29) * mm});
            skLineSegment(sketch, "E197", {"start": v(-669.33, 830.91) * mm, "end": v(-655.07, 830.91) * mm});
            skPoint(sketch, "E198.visualSharp", {"position": v(-616.97, 830.91) * mm});
            skArc(sketch, "E198.filletArc", {"start": v(-616.97, 792.81) * mm, "mid": v(-628.13, 819.75) * mm, "end": v(-655.07, 830.91) * mm});
            skLineSegment(sketch, "E199.bottom", {"start": v(-667.77, 748.36) * mm, "end": v(-649.73, 748.36) * mm});
            skLineSegment(sketch, "E199.top", {"start": v(-667.77, 799.16) * mm, "end": v(-649.73, 799.16) * mm});
            skLineSegment(sketch, "E199.left", {"start": v(-667.77, 748.36) * mm, "end": v(-667.77, 799.16) * mm});
            skLineSegment(sketch, "E199.right", {"start": v(-649.73, 748.36) * mm, "end": v(-649.73, 799.16) * mm});
            skLineSegment(sketch, "E200", {"start": v(-58.17, 729.59) * mm, "end": v(-58.17, 830.91) * mm});
            skLineSegment(sketch, "E201", {"start": v(-58.17, 830.91) * mm, "end": v(58.17, 830.91) * mm});
            skLineSegment(sketch, "E202", {"start": v(58.17, 830.91) * mm, "end": v(58.17, 729.59) * mm});
            skLineSegment(sketch, "E203", {"start": v(-58.17, 799.16) * mm, "end": v(-76.2, 799.16) * mm});
            skLineSegment(sketch, "E204", {"start": v(-76.2, 799.16) * mm, "end": v(-76.2, 748.36) * mm});
            skLineSegment(sketch, "E205", {"start": v(-76.2, 748.36) * mm, "end": v(-58.17, 748.36) * mm});
            skLineSegment(sketch, "E206", {"start": v(58.17, 799.16) * mm, "end": v(76.2, 799.16) * mm});
            skLineSegment(sketch, "E207", {"start": v(76.2, 799.16) * mm, "end": v(76.2, 748.36) * mm});
            skLineSegment(sketch, "E208", {"start": v(76.2, 748.36) * mm, "end": v(58.17, 748.36) * mm});
            skLineSegment(sketch, "E209", {"start": v(-775.2, -121.65) * mm, "end": v(-914.5, -111.34) * mm});
            skLineSegment(sketch, "E210", {"start": v(-914.5, -111.34) * mm, "end": v(-949.18, -579.96) * mm});
            skLineSegment(sketch, "E211", {"start": v(-949.18, -579.96) * mm, "end": v(-809.86, -590.27) * mm});
            skLineSegment(sketch, "E212", {"start": v(-835.86, -117.16) * mm, "end": v(-870.53, -585.78) * mm, "construction": true});
            skLineSegment(sketch, "E213.MirrorCS", {"start": v(-921.07, -200) * mm, "end": v(-916.38, -136.67) * mm});
            skLineSegment(sketch, "E214.MirrorCS", {"start": v(-903.08, -201.33) * mm, "end": v(-921.07, -200) * mm});
            skLineSegment(sketch, "E215.MirrorCS", {"start": v(-915.26, -365.98) * mm, "end": v(-933.25, -364.65) * mm});
            skLineSegment(sketch, "E216.MirrorCS", {"start": v(-933.25, -364.65) * mm, "end": v(-928.56, -301.32) * mm});
            skLineSegment(sketch, "E217.MirrorCS", {"start": v(-916.38, -136.67) * mm, "end": v(-898.4, -138) * mm});
            skLineSegment(sketch, "E218.MirrorCS", {"start": v(-928.56, -301.32) * mm, "end": v(-910.58, -302.65) * mm});
            skLineSegment(sketch, "E219", {"start": v(-898.4, -138) * mm, "end": v(-903.08, -201.33) * mm});
            skLineSegment(sketch, "E220", {"start": v(-910.58, -302.65) * mm, "end": v(-915.26, -365.98) * mm});
            skLineSegment(sketch, "E221", {"start": v(-912.92, -334.32) * mm, "end": v(-930.9, -332.99) * mm, "construction": true});
            skLineSegment(sketch, "E222.MirrorCS", {"start": v(-927.45, -530.63) * mm, "end": v(-922.76, -467.3) * mm});
            skLineSegment(sketch, "E223.MirrorCS", {"start": v(-922.76, -467.3) * mm, "end": v(-940.75, -465.97) * mm});
            skLineSegment(sketch, "E224.MirrorCS", {"start": v(-940.75, -465.97) * mm, "end": v(-945.43, -529.3) * mm});
            skLineSegment(sketch, "E225.MirrorCS", {"start": v(-945.43, -529.3) * mm, "end": v(-927.45, -530.63) * mm});
            skLineSegment(sketch, "E226", {"start": v(-1335.53, -494.64) * mm, "end": v(-1317.5, -494.64) * mm, "construction": true});
            skLineSegment(sketch, "E227.MirrorCS", {"start": v(-1335.53, -691.49) * mm, "end": v(-1317.5, -691.49) * mm});
            skLineSegment(sketch, "E228.MirrorCS", {"start": v(-1335.53, -627.99) * mm, "end": v(-1317.5, -627.99) * mm});
            skLineSegment(sketch, "E229.MirrorCS", {"start": v(-1335.53, -691.49) * mm, "end": v(-1335.53, -627.99) * mm});
            skLineSegment(sketch, "E230.MirrorCS", {"start": v(-1183.13, -691.49) * mm, "end": v(-1183.13, -627.99) * mm});
            skLineSegment(sketch, "E231.MirrorCS", {"start": v(-1183.13, -627.99) * mm, "end": v(-1201.17, -627.99) * mm});
            skLineSegment(sketch, "E232.MirrorCS", {"start": v(-1183.13, -691.49) * mm, "end": v(-1201.17, -691.49) * mm});
            skLineSegment(sketch, "E233", {"start": v(-946.37, -541.97) * mm, "end": v(-667.77, -562.58) * mm});
            skLineSegment(sketch, "E234", {"start": v(-947.7, -559.95) * mm, "end": v(-667.77, -580.66) * mm});
            skLineSegment(sketch, "E235", {"start": v(-946.37, -541.97) * mm, "end": v(-947.7, -559.95) * mm});
            skLineSegment(sketch, "E236.bottom", {"start": v(-67, -1246.22) * mm, "end": v(67.37, -1246.22) * mm});
            skLineSegment(sketch, "E236.top", {"start": v(-67, -989.94) * mm, "end": v(67.37, -989.94) * mm});
            skLineSegment(sketch, "E236.left", {"start": v(-67, -1246.22) * mm, "end": v(-67, -989.94) * mm});
            skLineSegment(sketch, "E236.right", {"start": v(67.37, -1246.22) * mm, "end": v(67.37, -989.94) * mm});
            skLineSegment(sketch, "E237", {"start": v(-67, -1415.39) * mm, "end": v(-76.2, -1415.39) * mm});
            skLineSegment(sketch, "E238", {"start": v(-76.2, -1415.39) * mm, "end": v(-76.2, -1555.09) * mm});
            skLineSegment(sketch, "E239", {"start": v(-76.2, -1555.09) * mm, "end": v(-67, -1555.09) * mm});
            skLineSegment(sketch, "E240", {"start": v(67.37, -1415.39) * mm, "end": v(76.2, -1415.39) * mm});
            skLineSegment(sketch, "E241", {"start": v(76.2, -1415.39) * mm, "end": v(76.2, -1555.09) * mm});
            skLineSegment(sketch, "E242", {"start": v(76.2, -1555.09) * mm, "end": v(67.37, -1555.09) * mm});
            skCircle(sketch, "E243", {"center": v(0, -1118.08) * mm, "radius": 19.05 * mm});
            skPoint(sketch, "E243.centerSnap0", {"position": v(67.37, -1118.08) * mm});
            skLineSegment(sketch, "E244", {"start": v(-667.77, -562.58) * mm, "end": v(-667.77, -580.66) * mm});
            skLineSegment(sketch, "E245", {"start": v(-439.17, -729.59) * mm, "end": v(-439.17, -747.62) * mm});
            skLineSegment(sketch, "E246", {"start": v(-439.17, -747.62) * mm, "end": v(-515.37, -747.62) * mm});
            skLineSegment(sketch, "E247", {"start": v(-515.37, -747.62) * mm, "end": v(-515.37, -729.59) * mm});
            skLineSegment(sketch, "E248", {"start": v(-820.17, -729.59) * mm, "end": v(-820.17, -747.62) * mm});
            skLineSegment(sketch, "E249", {"start": v(-820.17, -747.62) * mm, "end": v(-667.77, -747.62) * mm});
            skLineSegment(sketch, "E250", {"start": v(-667.77, -747.62) * mm, "end": v(-667.77, -729.59) * mm});
            skLineSegment(sketch, "E251", {"start": v(134.37, -729.59) * mm, "end": v(134.37, -747.62) * mm});
            skLineSegment(sketch, "E252", {"start": v(134.37, -747.62) * mm, "end": v(235.97, -747.62) * mm});
            skLineSegment(sketch, "E253", {"start": v(235.97, -747.62) * mm, "end": v(235.97, -729.59) * mm});
            skLineSegment(sketch, "E254.bottom", {"start": v(-1201.17, -881.99) * mm, "end": v(-540.77, -881.99) * mm});
            skLineSegment(sketch, "E254.top", {"start": v(-1201.17, -1440.79) * mm, "end": v(-540.77, -1440.79) * mm});
            skLineSegment(sketch, "E254.left", {"start": v(-1201.17, -881.99) * mm, "end": v(-1201.17, -1440.79) * mm});
            skLineSegment(sketch, "E254.right", {"start": v(-540.77, -881.99) * mm, "end": v(-540.77, -1161.39) * mm});
            skLineSegment(sketch, "E255", {"start": v(-1201.17, -1161.39) * mm, "end": v(-540.77, -1161.39) * mm, "construction": true});
            skLineSegment(sketch, "E256.bottom", {"start": v(-1099.57, -1085.19) * mm, "end": v(-947.17, -1085.19) * mm});
            skLineSegment(sketch, "E256.top", {"start": v(-1099.57, -1103.22) * mm, "end": v(-947.17, -1103.22) * mm});
            skLineSegment(sketch, "E256.left", {"start": v(-1099.57, -1085.19) * mm, "end": v(-1099.57, -1103.22) * mm});
            skLineSegment(sketch, "E256.right", {"start": v(-947.17, -1085.19) * mm, "end": v(-947.17, -1103.22) * mm});
            skLineSegment(sketch, "E257.MirrorCS", {"start": v(-718.57, -1085.19) * mm, "end": v(-718.57, -1103.22) * mm});
            skLineSegment(sketch, "E258.MirrorCS", {"start": v(-794.77, -1085.19) * mm, "end": v(-794.77, -1103.22) * mm});
            skLineSegment(sketch, "E259.MirrorCS", {"start": v(-718.57, -1085.19) * mm, "end": v(-794.77, -1085.19) * mm});
            skLineSegment(sketch, "E260.MirrorCS", {"start": v(-718.57, -1103.22) * mm, "end": v(-794.77, -1103.22) * mm});
            skLineSegment(sketch, "E261.MirrorCS", {"start": v(-947.17, -1237.59) * mm, "end": v(-947.17, -1219.55) * mm});
            skLineSegment(sketch, "E262.MirrorCS", {"start": v(-1099.57, -1237.59) * mm, "end": v(-1099.57, -1219.55) * mm});
            skLineSegment(sketch, "E263.MirrorCS", {"start": v(-1099.57, -1219.55) * mm, "end": v(-947.17, -1219.55) * mm});
            skLineSegment(sketch, "E264.MirrorCS", {"start": v(-1099.57, -1237.59) * mm, "end": v(-947.17, -1237.59) * mm});
            skLineSegment(sketch, "E265.bottom", {"start": v(-1016, -907.39) * mm, "end": v(-997.97, -907.39) * mm});
            skLineSegment(sketch, "E265.top", {"start": v(-1016, -1008.99) * mm, "end": v(-997.97, -1008.99) * mm});
            skLineSegment(sketch, "E265.left", {"start": v(-1016, -907.39) * mm, "end": v(-1016, -1008.99) * mm});
            skLineSegment(sketch, "E265.right", {"start": v(-997.97, -907.39) * mm, "end": v(-997.97, -1008.99) * mm});
            skLineSegment(sketch, "E266.MirrorCS", {"start": v(-1016, -1415.39) * mm, "end": v(-997.97, -1415.39) * mm});
            skLineSegment(sketch, "E267.MirrorCS", {"start": v(-1016, -1313.79) * mm, "end": v(-997.97, -1313.79) * mm});
            skLineSegment(sketch, "E268.MirrorCS", {"start": v(-1016, -1415.39) * mm, "end": v(-1016, -1313.79) * mm});
            skLineSegment(sketch, "E269.MirrorCS", {"start": v(-997.97, -1415.39) * mm, "end": v(-997.97, -1313.79) * mm});
            skLineSegment(sketch, "E270.MirrorCS", {"start": v(-794.77, -1237.59) * mm, "end": v(-794.77, -1219.55) * mm});
            skLineSegment(sketch, "E271.MirrorCS", {"start": v(-718.57, -1237.59) * mm, "end": v(-718.57, -1219.55) * mm});
            skLineSegment(sketch, "E272.MirrorCS", {"start": v(-718.57, -1237.59) * mm, "end": v(-794.77, -1237.59) * mm});
            skLineSegment(sketch, "E273.MirrorCS", {"start": v(-718.57, -1219.55) * mm, "end": v(-794.77, -1219.55) * mm});
            skLineSegment(sketch, "E274", {"start": v(-667.77, -1085.19) * mm, "end": v(-667.77, -1237.59) * mm});
            skLineSegment(sketch, "E275", {"start": v(-439.17, -729.59) * mm, "end": v(-401.07, -729.59) * mm});
            skLineSegment(sketch, "E276", {"start": v(-401.07, -729.59) * mm, "end": v(-401.07, -704.19) * mm});
            skFitSpline(sketch, "E277", {"points": [v(-566.17, -102.54) * mm, v(-401.07, -704.19) * mm], "startDerivative": vector(0, -1097.57) * mm, "endDerivative": vector(0, -707.38) * mm});
            skLineSegment(sketch, "E278", {"start": v(-667.77, -1085.19) * mm, "end": v(-540.77, -994.38) * mm});
            skLineSegment(sketch, "E279", {"start": v(-540.77, -1161.39) * mm, "end": v(-540.77, -1440.79) * mm});
            skLineSegment(sketch, "E280", {"start": v(-945.53, 392.79) * mm, "end": v(-1015.32, 374.58) * mm});
            skLineSegment(sketch, "E281", {"start": v(-945.53, 392.79) * mm, "end": v(-945.53, 373.74) * mm});
            skLineSegment(sketch, "E282", {"start": v(-945.53, 373.74) * mm, "end": v(-927.5, 373.74) * mm});
            skLineSegment(sketch, "E283", {"start": v(-927.5, 373.74) * mm, "end": v(-927.5, 291.19) * mm});
            skLineSegment(sketch, "E284", {"start": v(-927.5, 291.19) * mm, "end": v(-945.53, 291.19) * mm});
            skLineSegment(sketch, "E285", {"start": v(-945.53, 291.19) * mm, "end": v(-1091.58, 253.09) * mm});
            skLineSegment(sketch, "E286", {"start": v(-1047.13, 399.16) * mm, "end": v(-1047.13, 414.82) * mm});
            skLineSegment(sketch, "E287", {"start": v(-1024.88, 440.02) * mm, "end": v(-894.73, 456.29) * mm});
            skLineSegment(sketch, "E288", {"start": v(-894.73, 456.29) * mm, "end": v(-894.73, 472.67) * mm});
            skLineSegment(sketch, "E289", {"start": v(-894.73, 481.69) * mm, "end": v(-1053.48, 481.69) * mm, "construction": true});
            skLineSegment(sketch, "E290", {"start": v(-1091.58, 456.29) * mm, "end": v(-1091.58, 253.09) * mm});
            skPoint(sketch, "E291.visualSharp", {"position": v(-1091.58, 481.69) * mm});
            skPoint(sketch, "E292.visualSharp", {"position": v(-1047.13, 437.24) * mm});
            skArc(sketch, "E292.filletArc", {"start": v(-1024.88, 440.02) * mm, "mid": v(-1040.78, 431.63) * mm, "end": v(-1047.13, 414.82) * mm});
            skPoint(sketch, "E293.visualSharp", {"position": v(-1047.13, 366.28) * mm});
            skArc(sketch, "E293.filletArc", {"start": v(-1047.13, 399.16) * mm, "mid": v(-1037.26, 379.06) * mm, "end": v(-1015.32, 374.58) * mm});
            skLineSegment(sketch, "E294.bottom", {"start": v(-1053.48, 481.69) * mm, "end": v(-894.73, 481.69) * mm, "construction": true});
            skLineSegment(sketch, "E294.top", {"start": v(-1053.48, 472.67) * mm, "end": v(-894.73, 472.67) * mm});
            skLineSegment(sketch, "E294.left", {"start": v(-1053.48, 481.69) * mm, "end": v(-1053.48, 472.67) * mm});
            skLineSegment(sketch, "E294.right", {"start": v(-894.73, 481.69) * mm, "end": v(-894.73, 472.67) * mm, "construction": true});
            skLineSegment(sketch, "E295", {"start": v(-1091.58, 380.09) * mm, "end": v(-1109.62, 380.09) * mm});
            skLineSegment(sketch, "E296", {"start": v(-1109.62, 380.09) * mm, "end": v(-1109.62, 278.49) * mm});
            skLineSegment(sketch, "E297", {"start": v(-1109.62, 278.49) * mm, "end": v(-1091.58, 278.49) * mm});
            skPoint(sketch, "E298", {"position": v(-1109.62, 329.29) * mm});
            skLineSegment(sketch, "E299", {"start": v(-894.73, 472.67) * mm, "end": v(-894.73, 481.69) * mm, "construction": true});
            skLineSegment(sketch, "E300", {"start": v(-1053.48, 481.69) * mm, "end": v(-894.73, 472.67) * mm});
            skLineSegment(sketch, "E301", {"start": v(-1066.18, 481.69) * mm, "end": v(-1053.48, 481.69) * mm});
            skArc(sketch, "E302.filletArc", {"start": v(-1066.18, 481.69) * mm, "mid": v(-1084.14, 474.25) * mm, "end": v(-1091.58, 456.29) * mm});
            skSolve(sketch);
        }
        {
            var Q0;
            {var subQ3=sQuery(id+"F1.wireOp",EDGE,"E68");Q0=makeQuery(id+"F1.imprint","IMPRINT",FACE,{"disambiguationData":[TD([[makeQuery(id+"F1.imprint","IMPRINT",EDGE,{"derivedFrom":subQ3}),1.0]])]});}
            var Q1;
            {var subQ0=sQuery(id+"F1.wireOp",EDGE,"E72");Q1=makeQuery(id+"F1.imprint","IMPRINT",FACE,{"disambiguationData":[TD([[makeQuery(id+"F1.imprint","IMPRINT",EDGE,{"derivedFrom":subQ0}),-1.0]])]});}
            var Q2;
            {var subQ0=sQuery(id+"F1.wireOp",EDGE,"E75");Q2=makeQuery(id+"F1.imprint","IMPRINT",FACE,{"disambiguationData":[TD([[makeQuery(id+"F1.imprint","IMPRINT",EDGE,{"derivedFrom":subQ0}),-1.0]])]});}
            var Q3;
            {var subQ0=sQuery(id+"F1.wireOp",EDGE,"E64.MirrorCS");Q3=makeQuery(id+"F1.imprint","IMPRINT",FACE,{"disambiguationData":[TD([[makeQuery(id+"F1.imprint","IMPRINT",EDGE,{"derivedFrom":subQ0}),1.0]])]});}
            var Q4;
            Q4=makeQuery(id+"F1.imprint","IMPRINT",FACE,{"disambiguationData":[TD([[makeQuery(id+"F1.imprint","IMPRINT",EDGE,{"derivedFrom":sQuery(id+"F1.wireOp",EDGE,"E62.MirrorCS")}),-1.0]])]});
            var Q5;
            {var subQ0=sQuery(id+"F1.wireOp",EDGE,"E57.bottom");Q5=makeQuery(id+"F1.imprint","IMPRINT",FACE,{"disambiguationData":[TD([[makeQuery(id+"F1.imprint","IMPRINT",EDGE,{"derivedFrom":subQ0}),-1.0]])]});}
            var Q6;
            {var subQ0=sQuery(id+"F1.wireOp",EDGE,"E59.MirrorCS");Q6=makeQuery(id+"F1.imprint","IMPRINT",FACE,{"disambiguationData":[TD([[makeQuery(id+"F1.imprint","IMPRINT",EDGE,{"derivedFrom":subQ0}),1.0]])]});}
            var Q7;
            {var subQ11=sQuery(id+"F1.wireOp",EDGE,"E34");Q7=makeQuery(id+"F1.imprint","IMPRINT",FACE,{"disambiguationData":[TD([[makeQuery(id+"F1.imprint","IMPRINT",EDGE,{"derivedFrom":subQ11}),1.0]])]});}
            var Q8;
            {var subQ1=sQuery(id+"F1.wireOp",EDGE,"E96");Q8=makeQuery(id+"F1.imprint","IMPRINT",FACE,{"disambiguationData":[TD([[makeQuery(id+"F1.imprint","IMPRINT",EDGE,{"derivedFrom":subQ1}),-1.0]])]});}
            var Q9;
            Q9=makeQuery(id+"F1.imprint","IMPRINT",FACE,{"disambiguationData":[TD([[makeQuery(id+"F1.imprint","IMPRINT",EDGE,{"derivedFrom":sQuery(id+"F1.wireOp",EDGE,"E1.bottom")}),1.0]])]});
            var Q10;
            Q10=makeQuery(id+"F1.imprint","IMPRINT",FACE,{"disambiguationData":[TD([[makeQuery(id+"F1.imprint","IMPRINT",EDGE,{"derivedFrom":sQuery(id+"F1.wireOp",EDGE,"E2.bottom")}),1.0]])]});
            var Q11;
            Q11=makeQuery(id+"F1.imprint","IMPRINT",FACE,{"disambiguationData":[TD([[makeQuery(id+"F1.imprint","IMPRINT",EDGE,{"derivedFrom":sQuery(id+"F1.wireOp",EDGE,"E16.MirrorCS")}),1.0]])]});
            var Q12;
            Q12=makeQuery(id+"F1.imprint","IMPRINT",FACE,{"disambiguationData":[TD([[makeQuery(id+"F1.imprint","IMPRINT",EDGE,{"derivedFrom":sQuery(id+"F1.wireOp",EDGE,"E20.MirrorCS")}),1.0]])]});
            var Q13;
            Q13=makeQuery(id+"F1.imprint","IMPRINT",FACE,{"disambiguationData":[TD([[makeQuery(id+"F1.imprint","IMPRINT",EDGE,{"derivedFrom":sQuery(id+"F1.wireOp",EDGE,"E14.MirrorCS")}),1.0]])]});
            var Q14;
            Q14=makeQuery(id+"F1.imprint","IMPRINT",FACE,{"disambiguationData":[TD([[makeQuery(id+"F1.imprint","IMPRINT",EDGE,{"derivedFrom":sQuery(id+"F1.wireOp",EDGE,"E15.MirrorCS")}),1.0]])]});
            var Q15;
            Q15=makeQuery(id+"F1.imprint","IMPRINT",FACE,{"disambiguationData":[TD([[makeQuery(id+"F1.imprint","IMPRINT",EDGE,{"derivedFrom":sQuery(id+"F1.wireOp",EDGE,"E5.MirrorCS")}),-1.0]])]});
            var Q16;
            Q16=makeQuery(id+"F1.imprint","IMPRINT",FACE,{"disambiguationData":[TD([[makeQuery(id+"F1.imprint","IMPRINT",EDGE,{"derivedFrom":sQuery(id+"F1.wireOp",EDGE,"E7.MirrorCS")}),-1.0]])]});
            var Q17;
            Q17=makeQuery(id+"F1.imprint","IMPRINT",FACE,{"disambiguationData":[TD([[makeQuery(id+"F1.imprint","IMPRINT",EDGE,{"derivedFrom":sQuery(id+"F1.wireOp",EDGE,"E101.0")}),-1.0]])]});
            var Q18;
            Q18=makeQuery(id+"F1.imprint","IMPRINT",FACE,{"disambiguationData":[TD([[makeQuery(id+"F1.imprint","IMPRINT",EDGE,{"derivedFrom":sQuery(id+"F1.wireOp",EDGE,"E123")}),-1.0]])]});
            var Q19;
            {var subQ1=sQuery(id+"F1.wireOp",EDGE,"E149.top");Q19=makeQuery(id+"F1.imprint","IMPRINT",FACE,{"disambiguationData":[TD([[makeQuery(id+"F1.imprint","IMPRINT",EDGE,{"derivedFrom":subQ1}),1.0]])]});}
            var Q20;
            Q20=makeQuery(id+"F1.imprint","IMPRINT",FACE,{"disambiguationData":[TD([[makeQuery(id+"F1.imprint","IMPRINT",EDGE,{"derivedFrom":sQuery(id+"F1.wireOp",EDGE,"E163")}),1.0]])]});
            var Q21;
            {var subQ4=sQuery(id+"F1.wireOp",EDGE,"E118.right");Q21=makeQuery(id+"F1.imprint","IMPRINT",FACE,{"disambiguationData":[TD([[makeQuery(id+"F1.imprint","IMPRINT",EDGE,{"derivedFrom":subQ4}),1.0]])]});}
            var Q22;
            {var subQ0=sQuery(id+"F1.wireOp",EDGE,"E117.right");Q22=makeQuery(id+"F1.imprint","IMPRINT",FACE,{"disambiguationData":[TD([[makeQuery(id+"F1.imprint","IMPRINT",EDGE,{"derivedFrom":subQ0}),1.0]])]});}
            var Q23;
            {var subQ6=sQuery(id+"F1.wireOp",EDGE,"E117.left");Q23=makeQuery(id+"F1.imprint","IMPRINT",FACE,{"disambiguationData":[TD([[makeQuery(id+"F1.imprint","IMPRINT",EDGE,{"derivedFrom":subQ6}),-1.0]])]});}
            var Q24;
            {var subQ7=sQuery(id+"F1.wireOp",EDGE,"E183.bottom");Q24=makeQuery(id+"F1.imprint","IMPRINT",FACE,{"disambiguationData":[TD([[makeQuery(id+"F1.imprint","IMPRINT",EDGE,{"derivedFrom":subQ7}),-1.0]])]});}
            var Q25;
            {var subQ0=sQuery(id+"F1.wireOp",EDGE,"E180");Q25=makeQuery(id+"F1.imprint","IMPRINT",FACE,{"disambiguationData":[TD([[makeQuery(id+"F1.imprint","IMPRINT",EDGE,{"derivedFrom":subQ0}),1.0]])]});}
            var Q26;
            {var subQ12=sQuery(id+"F1.wireOp",EDGE,"E0.top");Q26=makeQuery(id+"F1.imprint","IMPRINT",FACE,{"disambiguationData":[TD([[makeQuery(id+"F1.imprint","IMPRINT",EDGE,{"derivedFrom":subQ12}),1.0]])]});}
            var Q27;
            {var subQ0=sQuery(id+"F1.wireOp",EDGE,"E203");Q27=makeQuery(id+"F1.imprint","IMPRINT",FACE,{"disambiguationData":[TD([[makeQuery(id+"F1.imprint","IMPRINT",EDGE,{"derivedFrom":subQ0}),1.0]])]});}
            var Q28;
            {var subQ0=sQuery(id+"F1.wireOp",EDGE,"E206");Q28=makeQuery(id+"F1.imprint","IMPRINT",FACE,{"disambiguationData":[TD([[makeQuery(id+"F1.imprint","IMPRINT",EDGE,{"derivedFrom":subQ0}),-1.0]])]});}
            var Q29;
            {var subQ6=sQuery(id+"F1.wireOp",EDGE,"E209");Q29=makeQuery(id+"F1.imprint","IMPRINT",FACE,{"disambiguationData":[TD([[makeQuery(id+"F1.imprint","IMPRINT",EDGE,{"derivedFrom":subQ6}),1.0]])]});}
            var Q30;
            {var subQ0=sQuery(id+"F1.wireOp",EDGE,"E211");Q30=makeQuery(id+"F1.imprint","IMPRINT",FACE,{"disambiguationData":[TD([[makeQuery(id+"F1.imprint","IMPRINT",EDGE,{"derivedFrom":subQ0}),1.0]])]});}
            var Q31;
            Q31=makeQuery(id+"F1.imprint","IMPRINT",FACE,{"disambiguationData":[TD([[makeQuery(id+"F1.imprint","IMPRINT",EDGE,{"derivedFrom":sQuery(id+"F1.wireOp",EDGE,"E236.bottom")}),1.0]])]});
            var Q32;
            {var subQ1=sQuery(id+"F1.wireOp",EDGE,"E56.bottom");Q32=makeQuery(id+"F1.imprint","IMPRINT",FACE,{"disambiguationData":[TD([[makeQuery(id+"F1.imprint","IMPRINT",EDGE,{"derivedFrom":subQ1}),-1.0]])]});}
            var Q33;
            {var subQ0=sQuery(id+"F1.wireOp",EDGE,"E227.MirrorCS");Q33=makeQuery(id+"F1.imprint","IMPRINT",FACE,{"disambiguationData":[TD([[makeQuery(id+"F1.imprint","IMPRINT",EDGE,{"derivedFrom":subQ0}),1.0]])]});}
            var Q34;
            Q34=makeQuery(id+"F1.imprint","IMPRINT",FACE,{"disambiguationData":[TD([[makeQuery(id+"F1.imprint","IMPRINT",EDGE,{"derivedFrom":sQuery(id+"F1.wireOp",EDGE,"E230.MirrorCS")}),1.0]])]});
            var Q35;
            {var subQ2=sQuery(id+"F1.wireOp",EDGE,"E240");Q35=makeQuery(id+"F1.imprint","IMPRINT",FACE,{"disambiguationData":[TD([[makeQuery(id+"F1.imprint","IMPRINT",EDGE,{"derivedFrom":subQ2}),-1.0]])]});}
            var Q36;
            {var subQ2=sQuery(id+"F1.wireOp",EDGE,"E237");Q36=makeQuery(id+"F1.imprint","IMPRINT",FACE,{"disambiguationData":[TD([[makeQuery(id+"F1.imprint","IMPRINT",EDGE,{"derivedFrom":subQ2}),1.0]])]});}
            var Q37;
            Q37=makeQuery(id+"F1.imprint","IMPRINT",FACE,{"disambiguationData":[TD([[makeQuery(id+"F1.imprint","IMPRINT",EDGE,{"derivedFrom":sQuery(id+"F1.wireOp",EDGE,"E254.bottom")}),-1.0]])]});
            var Q38;
            Q38=makeQuery(id+"F1.imprint","IMPRINT",FACE,{"disambiguationData":[TD([[makeQuery(id+"F1.imprint","IMPRINT",EDGE,{"derivedFrom":sQuery(id+"F1.wireOp",EDGE,"E34")}),-1.0]])]});
            var Q39;
            {var subQ0=sQuery(id+"F1.wireOp",EDGE,"E245");Q39=makeQuery(id+"F1.imprint","IMPRINT",FACE,{"disambiguationData":[TD([[makeQuery(id+"F1.imprint","IMPRINT",EDGE,{"derivedFrom":subQ0}),-1.0]])]});}
            var Q40;
            {var subQ0=sQuery(id+"F1.wireOp",EDGE,"E251");Q40=makeQuery(id+"F1.imprint","IMPRINT",FACE,{"disambiguationData":[TD([[makeQuery(id+"F1.imprint","IMPRINT",EDGE,{"derivedFrom":subQ0}),1.0]])]});}
            extrude(context, id + "F2", {"entities" : qUnion([Q0, Q1, Q2, Q3, Q4, Q5, Q6, Q7, Q8, Q9, Q10, Q11, Q12, Q13, Q14, Q15, Q16, Q17, Q18, Q19, Q20, Q21, Q22, Q23, Q24, Q25, Q26, Q27, Q28, Q29, Q30, Q31, Q32, Q33, Q34, Q35, Q36, Q37, Q38, Q39, Q40]), "depth" : (getVariable(context, 'ply34')) * mm});
        }
        {
            var Q0;
            {var subQ0=sQuery(id+"F1.wireOp",EDGE,"E117.left");Q0=makeQuery(id+"F1.imprint","IMPRINT",FACE,{"disambiguationData":[TD([[makeQuery(id+"F1.imprint","IMPRINT",EDGE,{"derivedFrom":subQ0}),1.0]])]});}
            var Q1;
            {var subQ0=sQuery(id+"F1.wireOp",EDGE,"E118.left");Q1=makeQuery(id+"F1.imprint","IMPRINT",FACE,{"disambiguationData":[TD([[makeQuery(id+"F1.imprint","IMPRINT",EDGE,{"derivedFrom":subQ0}),1.0]])]});}
            extrude(context, id + "F3", {"entities" : qUnion([Q0, Q1]), "operationType" : NewBodyOperationType.ADD, "depth" : (getVariable(context, 'ply34') / 2) * mm});
        }
        {
            var Q0;
            Q0=makeQuery(id+"F1.imprint","IMPRINT",FACE,{"disambiguationData":[TD([[makeQuery(id+"F1.imprint","IMPRINT",EDGE,{"derivedFrom":sQuery(id+"F1.wireOp",EDGE,"E135.bottom")}),-1.0]])]});
            extrude(context, id + "F4", {"entities" : qUnion([Q0]), "depth" : 68.58 * mm});
        }
        {
            var Q0;
            Q0=qCreatedBy(makeId("Front.planeOp"),FACE);
            var sketch = newSketch(context, id + "F5", { "sketchPlane" : qUnion([Q0])});
            skLineSegment(sketch, "E303.bottom", {"start": v(410.08, 63.5) * mm, "end": v(504.32, 63.5) * mm});
            skLineSegment(sketch, "E303.top", {"start": v(410.08, -63.5) * mm, "end": v(431.8, -63.5) * mm});
            skLineSegment(sketch, "E303.left", {"start": v(410.08, 63.5) * mm, "end": v(410.08, -63.5) * mm});
            skPoint(sketch, "E303.middle", {"position": v(457.2, 0) * mm});
            skLineSegment(sketch, "E304.bottom", {"start": v(448.18, 25.4) * mm, "end": v(466.22, 25.4) * mm});
            skLineSegment(sketch, "E304.top", {"start": v(448.18, -25.4) * mm, "end": v(466.22, -25.4) * mm});
            skLineSegment(sketch, "E304.left", {"start": v(448.18, 25.4) * mm, "end": v(448.18, -25.4) * mm});
            skLineSegment(sketch, "E304.right", {"start": v(466.22, 25.4) * mm, "end": v(466.22, -25.4) * mm});
            skLineSegment(sketch, "E305", {"start": v(517.02, 63.5) * mm, "end": v(517.02, -63.5) * mm});
            skLineSegment(sketch, "E306", {"start": v(504.32, 63.5) * mm, "end": v(517.02, 63.5) * mm});
            skLineSegment(sketch, "E307", {"start": v(517.02, -63.5) * mm, "end": v(504.32, -63.5) * mm});
            skLineSegment(sketch, "E308", {"start": v(410.08, 63.5) * mm, "end": v(392.05, 63.5) * mm});
            skLineSegment(sketch, "E309", {"start": v(392.05, 63.5) * mm, "end": v(392.05, 38.1) * mm});
            skLineSegment(sketch, "E310", {"start": v(392.05, 38.1) * mm, "end": v(410.08, 38.1) * mm});
            skLineSegment(sketch, "E311", {"start": v(410.08, 0) * mm, "end": v(517.02, 0) * mm, "construction": true});
            skLineSegment(sketch, "E312", {"start": v(517.02, 0) * mm, "end": v(463.55, 0) * mm, "construction": true});
            skLineSegment(sketch, "E313", {"start": v(463.55, 0) * mm, "end": v(463.55, 63.5) * mm, "construction": true});
            skLineSegment(sketch, "E314.MirrorCS", {"start": v(392.05, -38.1) * mm, "end": v(410.08, -38.1) * mm});
            skLineSegment(sketch, "E315.MirrorCS", {"start": v(392.05, -63.5) * mm, "end": v(392.05, -38.1) * mm});
            skLineSegment(sketch, "E316.MirrorCS", {"start": v(410.08, -63.5) * mm, "end": v(392.05, -63.5) * mm});
            skLineSegment(sketch, "E317.MirrorCS", {"start": v(517.02, 63.5) * mm, "end": v(535.05, 63.5) * mm});
            skLineSegment(sketch, "E318.MirrorCS", {"start": v(535.05, 63.5) * mm, "end": v(535.05, 38.1) * mm});
            skLineSegment(sketch, "E319.MirrorCS", {"start": v(535.05, 38.1) * mm, "end": v(517.02, 38.1) * mm});
            skLineSegment(sketch, "E320.MirrorCS", {"start": v(535.05, -63.5) * mm, "end": v(535.05, -38.1) * mm});
            skLineSegment(sketch, "E321.MirrorCS", {"start": v(517.02, -63.5) * mm, "end": v(535.05, -63.5) * mm});
            skLineSegment(sketch, "E322.MirrorCS", {"start": v(535.05, -38.1) * mm, "end": v(517.02, -38.1) * mm});
            skLineSegment(sketch, "E323.bottom", {"start": v(379.35, 38.1) * mm, "end": v(361.31, 38.1) * mm});
            skLineSegment(sketch, "E323.top", {"start": v(379.35, -38.1) * mm, "end": v(361.31, -38.1) * mm});
            skLineSegment(sketch, "E323.left", {"start": v(379.35, 38.1) * mm, "end": v(379.35, -38.1) * mm});
            skLineSegment(sketch, "E323.right", {"start": v(361.31, 38.1) * mm, "end": v(361.31, -38.1) * mm});
            skPoint(sketch, "E323.middle", {"position": v(370.33, 0) * mm});
            skLineSegment(sketch, "E324", {"start": v(361.31, 38.1) * mm, "end": v(361.31, 63.5) * mm});
            skLineSegment(sketch, "E325", {"start": v(361.31, 63.5) * mm, "end": v(334.33, 63.5) * mm});
            skLineSegment(sketch, "E326", {"start": v(334.33, 63.5) * mm, "end": v(334.33, -63.5) * mm});
            skLineSegment(sketch, "E327", {"start": v(334.33, -63.5) * mm, "end": v(361.31, -63.5) * mm});
            skLineSegment(sketch, "E328", {"start": v(361.31, -63.5) * mm, "end": v(361.31, -38.1) * mm});
            skLineSegment(sketch, "E329", {"start": v(334.33, 38.1) * mm, "end": v(316.3, 38.1) * mm});
            skLineSegment(sketch, "E330", {"start": v(316.3, 38.1) * mm, "end": v(316.3, 63.5) * mm});
            skLineSegment(sketch, "E331", {"start": v(316.3, 63.5) * mm, "end": v(334.33, 63.5) * mm});
            skLineSegment(sketch, "E332.MirrorCS", {"start": v(316.3, -63.5) * mm, "end": v(334.33, -63.5) * mm});
            skLineSegment(sketch, "E333.MirrorCS", {"start": v(316.3, -38.1) * mm, "end": v(316.3, -63.5) * mm});
            skLineSegment(sketch, "E334.MirrorCS", {"start": v(334.33, -38.1) * mm, "end": v(316.3, -38.1) * mm});
            skLineSegment(sketch, "E335", {"start": v(560.45, 25.4) * mm, "end": v(578.49, 25.4) * mm});
            skLineSegment(sketch, "E336", {"start": v(578.49, 25.4) * mm, "end": v(578.49, 63.5) * mm});
            skLineSegment(sketch, "E337", {"start": v(578.49, 63.5) * mm, "end": v(623.5, 63.5) * mm});
            skLineSegment(sketch, "E338", {"start": v(629.86, 57.15) * mm, "end": v(629.86, 57.15) * mm});
            skLineSegment(sketch, "E339", {"start": v(623.5, -444.5) * mm, "end": v(578.49, -444.5) * mm});
            skLineSegment(sketch, "E340", {"start": v(578.49, -444.5) * mm, "end": v(578.49, -406.4) * mm});
            skLineSegment(sketch, "E341", {"start": v(578.49, -25.4) * mm, "end": v(560.45, -25.4) * mm});
            skLineSegment(sketch, "E342", {"start": v(560.45, -25.4) * mm, "end": v(560.45, 25.4) * mm});
            skLineSegment(sketch, "E343.top", {"start": v(482.6, -444.5) * mm, "end": v(431.8, -444.5) * mm});
            skLineSegment(sketch, "E343.left", {"start": v(482.6, -63.5) * mm, "end": v(482.6, -444.5) * mm});
            skLineSegment(sketch, "E343.right", {"start": v(431.8, -63.5) * mm, "end": v(431.8, -444.5) * mm});
            skPoint(sketch, "E343.middle", {"position": v(457.2, -254) * mm});
            skLineSegment(sketch, "E344.trimOffspring", {"start": v(482.6, -63.5) * mm, "end": v(504.32, -63.5) * mm});
            skLineSegment(sketch, "E345.bottom", {"start": v(466.22, -355.6) * mm, "end": v(448.18, -355.6) * mm});
            skLineSegment(sketch, "E345.top", {"start": v(466.22, -406.4) * mm, "end": v(448.18, -406.4) * mm});
            skLineSegment(sketch, "E345.left", {"start": v(466.22, -355.6) * mm, "end": v(466.22, -406.4) * mm});
            skLineSegment(sketch, "E345.right", {"start": v(448.18, -355.6) * mm, "end": v(448.18, -406.4) * mm});
            skPoint(sketch, "E345.middle", {"position": v(457.2, -381) * mm});
            skLineSegment(sketch, "E346", {"start": v(578.49, -355.6) * mm, "end": v(560.45, -355.6) * mm});
            skLineSegment(sketch, "E347", {"start": v(560.45, -355.6) * mm, "end": v(560.45, -406.4) * mm});
            skLineSegment(sketch, "E348", {"start": v(560.45, -406.4) * mm, "end": v(578.49, -406.4) * mm});
            skLineSegment(sketch, "E349.trimOffspring", {"start": v(578.49, -355.6) * mm, "end": v(578.49, -25.4) * mm});
            skLineSegment(sketch, "E350", {"start": v(648.9, 38.1) * mm, "end": v(687, 38.1) * mm});
            skLineSegment(sketch, "E351", {"start": v(706.06, 57.15) * mm, "end": v(706.06, 57.15) * mm});
            skLineSegment(sketch, "E352", {"start": v(712.4, 63.5) * mm, "end": v(725.1, 63.5) * mm});
            skLineSegment(sketch, "E353", {"start": v(731.46, 57.15) * mm, "end": v(731.46, 50.8) * mm});
            skLineSegment(sketch, "E354", {"start": v(744.16, 38.1) * mm, "end": v(744.16, 38.1) * mm});
            skLineSegment(sketch, "E355", {"start": v(756.86, 50.8) * mm, "end": v(756.86, 57.15) * mm});
            skLineSegment(sketch, "E356", {"start": v(763.2, 63.5) * mm, "end": v(763.2, 63.5) * mm});
            skLineSegment(sketch, "E357", {"start": v(782.26, 44.45) * mm, "end": v(782.26, 12.7) * mm});
            skLineSegment(sketch, "E358", {"start": v(756.86, -12.7) * mm, "end": v(667.96, -12.7) * mm});
            skLineSegment(sketch, "E359", {"start": v(667.96, -88.9) * mm, "end": v(756.86, -88.9) * mm});
            skLineSegment(sketch, "E360", {"start": v(782.26, -114.3) * mm, "end": v(782.26, -120.65) * mm});
            skLineSegment(sketch, "E361", {"start": v(763.2, -139.7) * mm, "end": v(763.2, -139.7) * mm});
            skLineSegment(sketch, "E362", {"start": v(756.86, -133.35) * mm, "end": v(756.86, -127) * mm});
            skPoint(sketch, "E362.endSnap0", {"position": v(782.26, -114.3) * mm});
            skLineSegment(sketch, "E363", {"start": v(744.16, -114.3) * mm, "end": v(744.16, -114.3) * mm});
            skLineSegment(sketch, "E364", {"start": v(731.46, -127) * mm, "end": v(731.46, -133.35) * mm});
            skLineSegment(sketch, "E365", {"start": v(725.1, -139.7) * mm, "end": v(667.96, -139.7) * mm});
            skLineSegment(sketch, "E366", {"start": v(648.9, -419.1) * mm, "end": v(687, -419.1) * mm});
            skLineSegment(sketch, "E367", {"start": v(706.06, -438.15) * mm, "end": v(706.06, -438.15) * mm});
            skLineSegment(sketch, "E368", {"start": v(712.4, -444.5) * mm, "end": v(712.4, -444.5) * mm});
            skLineSegment(sketch, "E369", {"start": v(731.46, -425.45) * mm, "end": v(731.46, -393.7) * mm});
            skLineSegment(sketch, "E370", {"start": v(706.06, -368.3) * mm, "end": v(667.96, -368.3) * mm});
            skLineSegment(sketch, "E371.trimOffspring", {"start": v(629.86, -50.8) * mm, "end": v(629.86, -50.8) * mm});
            skLineSegment(sketch, "E372.trimOffspring", {"start": v(629.86, -177.8) * mm, "end": v(629.86, -330.2) * mm});
            skLineSegment(sketch, "E373.trimOffspring", {"start": v(629.86, -438.15) * mm, "end": v(629.86, -438.15) * mm});
            skPoint(sketch, "E374.visualSharp", {"position": v(629.86, 38.1) * mm});
            skArc(sketch, "E374.filletArc", {"start": v(629.86, 57.15) * mm, "mid": v(635.44, 43.68) * mm, "end": v(648.9, 38.1) * mm});
            skPoint(sketch, "E375.visualSharp", {"position": v(706.06, 38.1) * mm});
            skArc(sketch, "E375.filletArc", {"start": v(687, 38.1) * mm, "mid": v(700.48, 43.68) * mm, "end": v(706.06, 57.15) * mm});
            skPoint(sketch, "E376.visualSharp", {"position": v(731.46, 38.1) * mm});
            skArc(sketch, "E376.filletArc", {"start": v(731.46, 50.8) * mm, "mid": v(735.18, 41.82) * mm, "end": v(744.16, 38.1) * mm});
            skPoint(sketch, "E377.visualSharp", {"position": v(756.86, 38.1) * mm});
            skArc(sketch, "E377.filletArc", {"start": v(744.16, 38.1) * mm, "mid": v(753.14, 41.82) * mm, "end": v(756.86, 50.8) * mm});
            skPoint(sketch, "E378.visualSharp", {"position": v(731.46, -114.3) * mm});
            skArc(sketch, "E378.filletArc", {"start": v(744.16, -114.3) * mm, "mid": v(735.18, -118.02) * mm, "end": v(731.46, -127) * mm});
            skPoint(sketch, "E379.visualSharp", {"position": v(756.86, -114.3) * mm});
            skArc(sketch, "E379.filletArc", {"start": v(756.86, -127) * mm, "mid": v(753.14, -118.02) * mm, "end": v(744.16, -114.3) * mm});
            skPoint(sketch, "E380.visualSharp", {"position": v(706.06, 63.5) * mm});
            skArc(sketch, "E380.filletArc", {"start": v(712.4, 63.5) * mm, "mid": v(707.92, 61.64) * mm, "end": v(706.06, 57.15) * mm});
            skPoint(sketch, "E381.visualSharp", {"position": v(731.46, 63.5) * mm});
            skArc(sketch, "E381.filletArc", {"start": v(731.46, 57.15) * mm, "mid": v(729.6, 61.64) * mm, "end": v(725.1, 63.5) * mm});
            skPoint(sketch, "E382.visualSharp", {"position": v(756.86, 63.5) * mm});
            skArc(sketch, "E382.filletArc", {"start": v(763.2, 63.5) * mm, "mid": v(758.72, 61.64) * mm, "end": v(756.86, 57.15) * mm});
            skPoint(sketch, "E383.visualSharp", {"position": v(629.86, 63.5) * mm});
            skArc(sketch, "E383.filletArc", {"start": v(629.86, 57.15) * mm, "mid": v(628, 61.64) * mm, "end": v(623.5, 63.5) * mm});
            skPoint(sketch, "E384.visualSharp", {"position": v(756.86, -139.7) * mm});
            skArc(sketch, "E384.filletArc", {"start": v(756.86, -133.35) * mm, "mid": v(758.72, -137.84) * mm, "end": v(763.2, -139.7) * mm});
            skPoint(sketch, "E385.visualSharp", {"position": v(731.46, -139.7) * mm});
            skArc(sketch, "E385.filletArc", {"start": v(725.1, -139.7) * mm, "mid": v(729.6, -137.84) * mm, "end": v(731.46, -133.35) * mm});
            skPoint(sketch, "E386.visualSharp", {"position": v(706.06, -444.5) * mm});
            skArc(sketch, "E386.filletArc", {"start": v(706.06, -438.15) * mm, "mid": v(707.92, -442.64) * mm, "end": v(712.4, -444.5) * mm});
            skPoint(sketch, "E387.visualSharp", {"position": v(629.86, -444.5) * mm});
            skArc(sketch, "E387.filletArc", {"start": v(623.5, -444.5) * mm, "mid": v(628, -442.64) * mm, "end": v(629.86, -438.15) * mm});
            skPoint(sketch, "E388.visualSharp", {"position": v(629.86, -419.1) * mm});
            skArc(sketch, "E388.filletArc", {"start": v(648.9, -419.1) * mm, "mid": v(635.44, -424.68) * mm, "end": v(629.86, -438.15) * mm});
            skPoint(sketch, "E389.visualSharp", {"position": v(706.06, -419.1) * mm});
            skArc(sketch, "E389.filletArc", {"start": v(706.06, -438.15) * mm, "mid": v(700.48, -424.68) * mm, "end": v(687, -419.1) * mm});
            skPoint(sketch, "E390.visualSharp", {"position": v(731.46, -444.5) * mm});
            skArc(sketch, "E390.filletArc", {"start": v(712.4, -444.5) * mm, "mid": v(725.88, -438.92) * mm, "end": v(731.46, -425.45) * mm});
            skPoint(sketch, "E391.visualSharp", {"position": v(731.46, -368.3) * mm});
            skArc(sketch, "E391.filletArc", {"start": v(731.46, -393.7) * mm, "mid": v(724.02, -375.74) * mm, "end": v(706.06, -368.3) * mm});
            skPoint(sketch, "E392.visualSharp", {"position": v(782.26, -88.9) * mm});
            skArc(sketch, "E392.filletArc", {"start": v(782.26, -114.3) * mm, "mid": v(774.82, -96.34) * mm, "end": v(756.86, -88.9) * mm});
            skPoint(sketch, "E393.visualSharp", {"position": v(782.26, -12.7) * mm});
            skArc(sketch, "E393.filletArc", {"start": v(756.86, -12.7) * mm, "mid": v(774.82, -5.26) * mm, "end": v(782.26, 12.7) * mm});
            skPoint(sketch, "E394.visualSharp", {"position": v(782.26, 63.5) * mm});
            skArc(sketch, "E394.filletArc", {"start": v(782.26, 44.45) * mm, "mid": v(776.68, 57.92) * mm, "end": v(763.2, 63.5) * mm});
            skPoint(sketch, "E395.visualSharp", {"position": v(782.26, -139.7) * mm});
            skArc(sketch, "E395.filletArc", {"start": v(763.2, -139.7) * mm, "mid": v(776.68, -134.12) * mm, "end": v(782.26, -120.65) * mm});
            skPoint(sketch, "E396.visualSharp", {"position": v(629.86, -12.7) * mm});
            skArc(sketch, "E396.filletArc", {"start": v(667.96, -12.7) * mm, "mid": v(641.02, -23.86) * mm, "end": v(629.86, -50.8) * mm});
            skPoint(sketch, "E397.visualSharp", {"position": v(629.86, -88.9) * mm});
            skArc(sketch, "E397.filletArc", {"start": v(629.86, -50.8) * mm, "mid": v(641.02, -77.74) * mm, "end": v(667.96, -88.9) * mm});
            skPoint(sketch, "E398.visualSharp", {"position": v(629.86, -139.7) * mm});
            skArc(sketch, "E398.filletArc", {"start": v(667.96, -139.7) * mm, "mid": v(641.02, -150.86) * mm, "end": v(629.86, -177.8) * mm});
            skPoint(sketch, "E399.visualSharp", {"position": v(629.86, -368.3) * mm});
            skArc(sketch, "E399.filletArc", {"start": v(629.86, -330.2) * mm, "mid": v(641.02, -357.14) * mm, "end": v(667.96, -368.3) * mm});
            skLineSegment(sketch, "E400.bottom", {"start": v(392.05, 88.9) * mm, "end": v(535.05, 88.9) * mm});
            skLineSegment(sketch, "E400.top", {"start": v(392.05, 215.9) * mm, "end": v(535.05, 215.9) * mm});
            skLineSegment(sketch, "E400.left", {"start": v(392.05, 88.9) * mm, "end": v(392.05, 215.9) * mm});
            skLineSegment(sketch, "E400.right", {"start": v(535.05, 88.9) * mm, "end": v(535.05, 215.9) * mm});
            skPoint(sketch, "E400.middle", {"position": v(463.55, 152.4) * mm});
            skLineSegment(sketch, "E401.bottom", {"start": v(392.05, 215.9) * mm, "end": v(410.08, 215.9) * mm});
            skLineSegment(sketch, "E401.top", {"start": v(392.05, 190.5) * mm, "end": v(410.08, 190.5) * mm});
            skLineSegment(sketch, "E401.left", {"start": v(392.05, 215.9) * mm, "end": v(392.05, 190.5) * mm});
            skLineSegment(sketch, "E401.right", {"start": v(410.08, 215.9) * mm, "end": v(410.08, 190.5) * mm});
            skPoint(sketch, "E401.middle", {"position": v(401.07, 203.2) * mm});
            skPoint(sketch, "E401.middle.positionSnap0", {"position": v(401.07, 63.5) * mm});
            skPoint(sketch, "E401.centerSnap0", {"position": v(401.07, 63.5) * mm});
            skLineSegment(sketch, "E402", {"start": v(392.05, 152.4) * mm, "end": v(535.05, 152.4) * mm, "construction": true});
            skPoint(sketch, "E403.MirrorP", {"position": v(401.07, 101.6) * mm});
            skLineSegment(sketch, "E404.MirrorCS", {"start": v(392.05, 88.9) * mm, "end": v(392.05, 114.3) * mm});
            skLineSegment(sketch, "E405.MirrorCS", {"start": v(392.05, 114.3) * mm, "end": v(410.08, 114.3) * mm});
            skLineSegment(sketch, "E406.MirrorCS", {"start": v(410.08, 88.9) * mm, "end": v(410.08, 114.3) * mm});
            skLineSegment(sketch, "E407.MirrorCS", {"start": v(392.05, 88.9) * mm, "end": v(410.08, 88.9) * mm});
            skPoint(sketch, "E408.MirrorP", {"position": v(526.03, 203.2) * mm});
            skLineSegment(sketch, "E409.MirrorCS", {"start": v(517.02, 215.9) * mm, "end": v(517.02, 190.5) * mm});
            skLineSegment(sketch, "E410.MirrorCS", {"start": v(535.05, 215.9) * mm, "end": v(535.05, 190.5) * mm});
            skLineSegment(sketch, "E411.MirrorCS", {"start": v(535.05, 190.5) * mm, "end": v(517.02, 190.5) * mm});
            skLineSegment(sketch, "E412.MirrorCS", {"start": v(535.05, 215.9) * mm, "end": v(517.02, 215.9) * mm});
            skPoint(sketch, "E413.MirrorP", {"position": v(526.03, 63.5) * mm});
            skLineSegment(sketch, "E414.MirrorCS", {"start": v(535.05, 114.3) * mm, "end": v(517.02, 114.3) * mm});
            skLineSegment(sketch, "E415.MirrorCS", {"start": v(517.02, 88.9) * mm, "end": v(517.02, 114.3) * mm});
            skPoint(sketch, "E416.MirrorP", {"position": v(526.03, 101.6) * mm});
            skLineSegment(sketch, "E417.MirrorCS", {"start": v(535.05, 88.9) * mm, "end": v(535.05, 114.3) * mm});
            skLineSegment(sketch, "E418.MirrorCS", {"start": v(535.05, 88.9) * mm, "end": v(517.02, 88.9) * mm});
            skLineSegment(sketch, "E419.bottom", {"start": v(448.18, 88.9) * mm, "end": v(466.22, 88.9) * mm});
            skLineSegment(sketch, "E419.top", {"start": v(448.18, 215.9) * mm, "end": v(466.22, 215.9) * mm});
            skLineSegment(sketch, "E419.left", {"start": v(448.18, 88.9) * mm, "end": v(448.18, 215.9) * mm});
            skLineSegment(sketch, "E419.right", {"start": v(466.22, 88.9) * mm, "end": v(466.22, 215.9) * mm});
            skPoint(sketch, "E419.middle", {"position": v(457.2, 152.4) * mm});
            skPoint(sketch, "E419.middle.positionSnap0", {"position": v(457.2, 63.5) * mm});
            skPoint(sketch, "E419.centerSnap0", {"position": v(457.2, 63.5) * mm});
            skLineSegment(sketch, "E420", {"start": v(448.18, 248.2) * mm, "end": v(431.8, 248.2) * mm});
            skLineSegment(sketch, "E421", {"start": v(431.8, 248.2) * mm, "end": v(431.8, 230.16) * mm});
            skLineSegment(sketch, "E422", {"start": v(431.8, 230.16) * mm, "end": v(392.05, 230.16) * mm});
            skLineSegment(sketch, "E423", {"start": v(392.05, 230.16) * mm, "end": v(392.05, 293.22) * mm});
            skLineSegment(sketch, "E424", {"start": v(392.05, 293.22) * mm, "end": v(448.18, 293.22) * mm});
            skLineSegment(sketch, "E425", {"start": v(448.18, 293.22) * mm, "end": v(448.18, 248.2) * mm});
            skLineSegment(sketch, "E426", {"start": v(466.22, 293.22) * mm, "end": v(535.05, 293.22) * mm});
            skLineSegment(sketch, "E427", {"start": v(535.05, 293.22) * mm, "end": v(535.05, 230.16) * mm});
            skLineSegment(sketch, "E428", {"start": v(535.05, 230.16) * mm, "end": v(482.6, 230.16) * mm});
            skLineSegment(sketch, "E429", {"start": v(482.6, 230.16) * mm, "end": v(482.6, 248.2) * mm});
            skLineSegment(sketch, "E430", {"start": v(482.6, 248.2) * mm, "end": v(466.22, 248.2) * mm});
            skLineSegment(sketch, "E431", {"start": v(466.22, 248.2) * mm, "end": v(466.22, 293.22) * mm});
            skSolve(sketch);
        }
        {
            var Q0;
            Q0=makeQuery(id+"F5.imprint","IMPRINT",FACE,{"disambiguationData":[TD([[makeQuery(id+"F5.imprint","IMPRINT",EDGE,{"derivedFrom":sQuery(id+"F5.wireOp",EDGE,"E400.left")}),-1.0]])]});
            var Q1;
            Q1=makeQuery(id+"F5.imprint","IMPRINT",FACE,{"disambiguationData":[TD([[makeQuery(id+"F5.imprint","IMPRINT",EDGE,{"derivedFrom":sQuery(id+"F5.wireOp",EDGE,"E400.right")}),1.0]])]});
            var Q2;
            {var subQ6=sQuery(id+"F5.wireOp",EDGE,"E303.bottom");Q2=makeQuery(id+"F5.imprint","IMPRINT",FACE,{"disambiguationData":[TD([[makeQuery(id+"F5.imprint","IMPRINT",EDGE,{"derivedFrom":subQ6}),-1.0]])]});}
            var Q3;
            {var subQ0=sQuery(id+"F5.wireOp",EDGE,"E308");Q3=makeQuery(id+"F5.imprint","IMPRINT",FACE,{"disambiguationData":[TD([[makeQuery(id+"F5.imprint","IMPRINT",EDGE,{"derivedFrom":subQ0}),1.0]])]});}
            var Q4;
            {var subQ2=sQuery(id+"F5.wireOp",EDGE,"E314.MirrorCS");Q4=makeQuery(id+"F5.imprint","IMPRINT",FACE,{"disambiguationData":[TD([[makeQuery(id+"F5.imprint","IMPRINT",EDGE,{"derivedFrom":subQ2}),-1.0]])]});}
            var Q5;
            Q5=makeQuery(id+"F5.imprint","IMPRINT",FACE,{"disambiguationData":[TD([[makeQuery(id+"F5.imprint","IMPRINT",EDGE,{"derivedFrom":sQuery(id+"F5.wireOp",EDGE,"E320.MirrorCS")}),1.0]])]});
            var Q6;
            {var subQ0=sQuery(id+"F5.wireOp",EDGE,"E317.MirrorCS");Q6=makeQuery(id+"F5.imprint","IMPRINT",FACE,{"disambiguationData":[TD([[makeQuery(id+"F5.imprint","IMPRINT",EDGE,{"derivedFrom":subQ0}),-1.0]])]});}
            var Q7;
            Q7=makeQuery(id+"F5.imprint","IMPRINT",FACE,{"disambiguationData":[TD([[makeQuery(id+"F5.imprint","IMPRINT",EDGE,{"derivedFrom":sQuery(id+"F5.wireOp",EDGE,"E323.right")}),-1.0]])]});
            var Q8;
            {var subQ2=sQuery(id+"F5.wireOp",EDGE,"E329");Q8=makeQuery(id+"F5.imprint","IMPRINT",FACE,{"disambiguationData":[TD([[makeQuery(id+"F5.imprint","IMPRINT",EDGE,{"derivedFrom":subQ2}),-1.0]])]});}
            var Q9;
            {var subQ0=sQuery(id+"F5.wireOp",EDGE,"E332.MirrorCS");Q9=makeQuery(id+"F5.imprint","IMPRINT",FACE,{"disambiguationData":[TD([[makeQuery(id+"F5.imprint","IMPRINT",EDGE,{"derivedFrom":subQ0}),1.0]])]});}
            var Q10;
            Q10=makeQuery(id+"F5.imprint","IMPRINT",FACE,{"disambiguationData":[TD([[makeQuery(id+"F5.imprint","IMPRINT",EDGE,{"derivedFrom":sQuery(id+"F5.wireOp",EDGE,"E323.bottom")}),1.0]])]});
            var Q11;
            Q11=makeQuery(id+"F5.imprint","IMPRINT",FACE,{"disambiguationData":[TD([[makeQuery(id+"F5.imprint","IMPRINT",EDGE,{"derivedFrom":sQuery(id+"F5.wireOp",EDGE,"E335")}),-1.0]])]});
            var Q12;
            Q12=makeQuery(id+"F5.imprint","IMPRINT",FACE,{"disambiguationData":[TD([[makeQuery(id+"F5.imprint","IMPRINT",EDGE,{"derivedFrom":sQuery(id+"F5.wireOp",EDGE,"E420")}),-1.0]])]});
            var Q13;
            Q13=makeQuery(id+"F5.imprint","IMPRINT",FACE,{"disambiguationData":[TD([[makeQuery(id+"F5.imprint","IMPRINT",EDGE,{"derivedFrom":sQuery(id+"F5.wireOp",EDGE,"E426")}),-1.0]])]});
            extrude(context, id + "F6", {"entities" : qUnion([Q0, Q1, Q2, Q3, Q4, Q5, Q6, Q7, Q8, Q9, Q10, Q11, Q12, Q13]), "depth" : (getVariable(context, 'ply34')) * mm});
        }
    });
